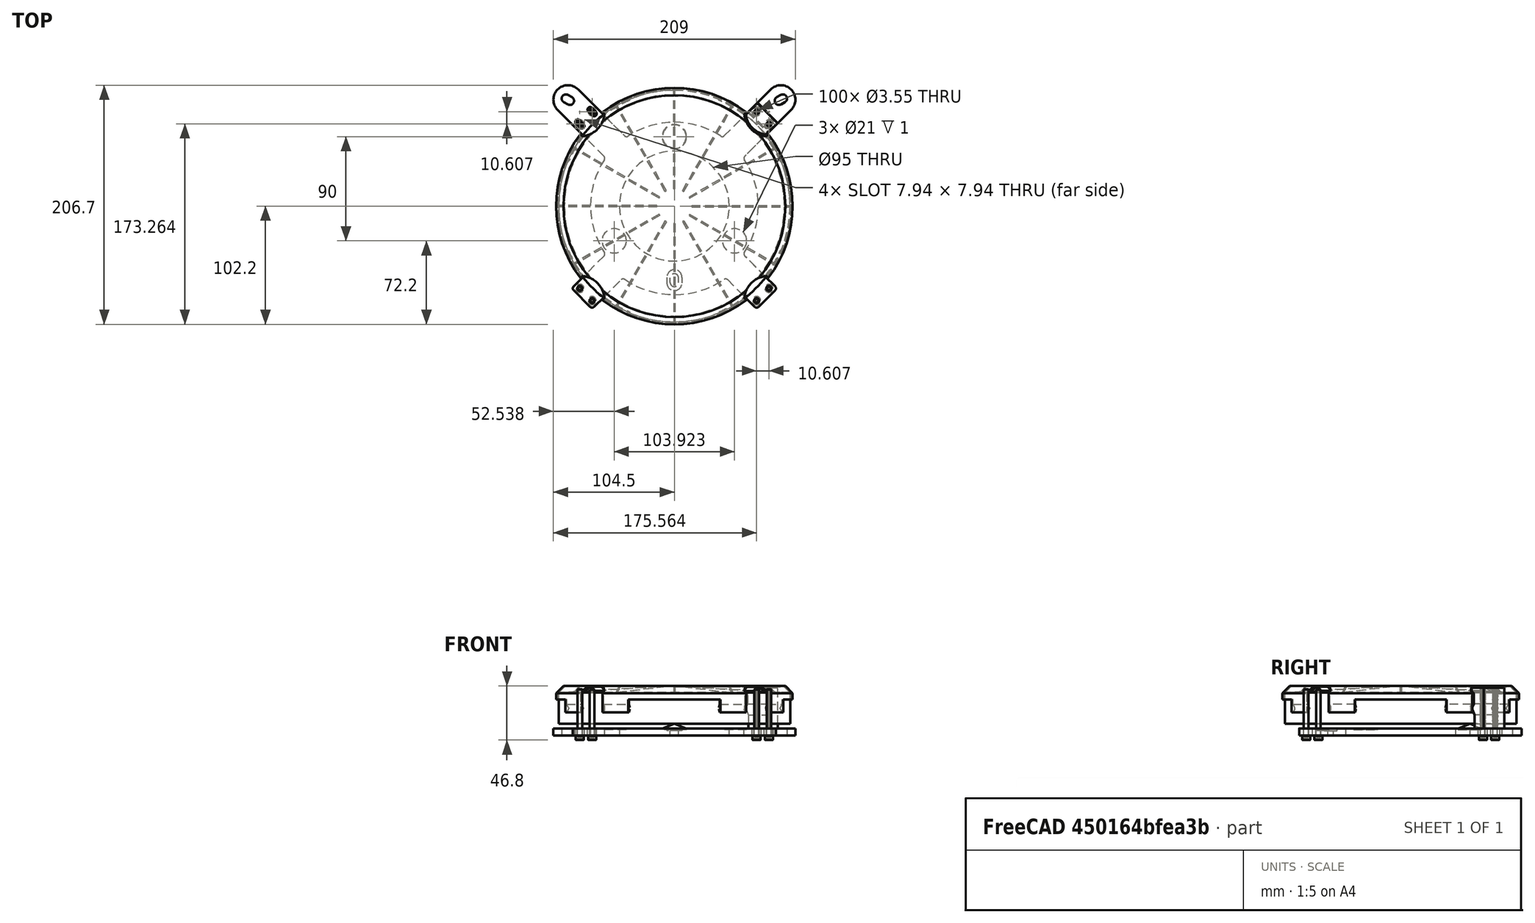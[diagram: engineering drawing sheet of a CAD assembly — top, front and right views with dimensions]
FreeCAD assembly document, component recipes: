
FREECAD ASSEMBLY — COMPONENT RECIPES ("PrimaryMirrorCell")

This assembly document has 5 components, labeled P0..P4 below (a component is one placed body or linked part). 5 of them carry a construction recipe — the FreeCAD feature program that regenerates the part from scratch, quoted from this document or its linked companion documents; the rest are supplied as boundary geometry only. No exploded tour is included for this assembly.
COMPONENT P0 — recipe-attached ("UpperCell", modeled in this document).
Construction recipe (the document's own serialized feature program — sketch geometry with constraints, then the solid features built on it; lengths are millimeters unless a unit is written):

FEATURE [Sketcher::SketchObject] Sketch  label="UpperCell_Base_Sketch"
  FullyConstrained = true
  MapMode = 5
  Support = -> [XY_Plane001]
  expr: Constraints[101] = <<Common>>#<<Parameters>>.collslot
  expr: Constraints[126] = <<Common>>#<<Parameters>>.collbolt * 1.1 + <<Common>>#<<Parameters>>.collextra * 2
  expr: Constraints[31] = <<Common>>#<<Parameters>>.rbracepos + <<Common>>#<<Parameters>>.pri_fwidth / 2
  expr: Constraints[35] = <<Common>>#<<Parameters>>.pri_fwidth
  expr: Constraints[50] = <<Common>>#<<Parameters>>.cpointpos + <<Common>>#<<Parameters>>.pri_fwidth / 2
  expr: Constraints[52] = <<Common>>#<<Parameters>>.pri_mdia / 2 + <<Common>>#<<Parameters>>.pri_mpad_z + <<Common>>#<<Parameters>>.clipwidth
  expr: Constraints[59] = <<Common>>#<<Parameters>>.rbracepos - <<Common>>#<<Parameters>>.pri_fwidth / 2
  expr: Constraints[61] = <<Common>>#<<Parameters>>.rbracepos
  expr: Constraints[76] = -<<Common>>#<<Parameters>>.cpointpos
  expr: Constraints[85] = <<Common>>#<<Parameters>>.collbolt * 1.2
  expr: Constraints[88] = <<Common>>#<<Parameters>>.collpos_y
  sketch-geometry (48):
    g0: LineSegment StartX=-79.9031 StartY=-79.9031 StartZ=0 EndX=92 EndY=92 EndZ=0
    g1: LineSegment StartX=79.9031 StartY=-79.9031 StartZ=0 EndX=-92 EndY=92 EndZ=0
    g2: LineSegment StartX=-59.3364 StartY=-41.6587 StartZ=0 EndX=-88.7419 EndY=-71.0642 EndZ=0
    g3: LineSegment StartX=-88.7419 StartY=-71.0642 StartZ=0 EndX=-71.0642 EndY=-88.7419 EndZ=0
    g4: LineSegment StartX=-71.0642 StartY=-88.7419 StartZ=0 EndX=-44.5278 EndY=-62.2055 EndZ=0
    g5: LineSegment StartX=44.5278 StartY=-62.2055 StartZ=0 EndX=71.0642 EndY=-88.7419 EndZ=0
    g6: LineSegment StartX=71.0642 StartY=-88.7419 StartZ=0 EndX=88.7419 EndY=-71.0642 EndZ=0
    g7: LineSegment StartX=88.7419 StartY=-71.0642 StartZ=0 EndX=59.3364 EndY=-41.6587 EndZ=0
    g8: LineSegment StartX=-59.3364 StartY=41.6587 StartZ=0 EndX=-100.839 EndY=83.1612 EndZ=0
    g9: LineSegment StartX=-100.839 StartY=83.1612 StartZ=0 EndX=-83.1612 EndY=100.839 EndZ=0
    g10: LineSegment StartX=-83.1612 StartY=100.839 StartZ=0 EndX=-41.6587 EndY=59.3364 EndZ=0
    g11: LineSegment StartX=41.6587 StartY=59.3364 StartZ=0 EndX=83.1612 EndY=100.839 EndZ=0
    g12: LineSegment StartX=83.1612 StartY=100.839 StartZ=0 EndX=100.839 EndY=83.1612 EndZ=0
    g13: LineSegment StartX=100.839 StartY=83.1612 StartZ=0 EndX=59.3364 EndY=41.6587 EndZ=0
    g14: ArcOfCircle CenterX=0 CenterY=0 CenterZ=0 NormalX=0 NormalY=0 NormalZ=1 AngleXU=0 Radius=72.5 StartAngle=2.52947 EndAngle=3.75371
    g15: ArcOfCircle CenterX=0 CenterY=0 CenterZ=0 NormalX=0 NormalY=0 NormalZ=1 AngleXU=0 Radius=72.5 StartAngle=5.67107 EndAngle=6.8953
    g16: ArcOfCircle CenterX=0 CenterY=0 CenterZ=0 NormalX=0 NormalY=0 NormalZ=1 AngleXU=0 Radius=72.5 StartAngle=0.958678 EndAngle=2.18291
    g17: ArcOfCircle CenterX=-92 CenterY=92 CenterZ=0 NormalX=0 NormalY=0 NormalZ=1 AngleXU=0 Radius=12.5 StartAngle=0.785398 EndAngle=3.92699
    g18: ArcOfCircle CenterX=92 CenterY=92 CenterZ=0 NormalX=0 NormalY=0 NormalZ=1 AngleXU=0 Radius=12.5 StartAngle=5.49779 EndAngle=8.63938
    g19: ArcOfCircle CenterX=0 CenterY=0 CenterZ=0 NormalX=0 NormalY=0 NormalZ=1 AngleXU=0 Radius=76.5 StartAngle=4.09113 EndAngle=5.33365
    g20: Circle CenterX=0 CenterY=0 CenterZ=0 NormalX=0 NormalY=0 NormalZ=1 AngleXU=0 Radius=47.5
    g21: Circle CenterX=0 CenterY=0 CenterZ=0 NormalX=0 NormalY=0 NormalZ=1 AngleXU=0 Radius=60
    g22: ArcOfCircle CenterX=-93.7367 CenterY=92.992 CenterZ=0 NormalX=0 NormalY=0 NormalZ=1 AngleXU=0 Radius=3.6 StartAngle=1.05182 EndAngle=4.19341
    g23: ArcOfCircle CenterX=-90.2633 CenterY=91.008 CenterZ=0 NormalX=0 NormalY=0 NormalZ=1 AngleXU=0 Radius=3.6 StartAngle=4.19341 EndAngle=7.33501
    g24: LineSegment StartX=-95.5222 StartY=89.866 StartZ=0 EndX=-92.0489 EndY=87.882 EndZ=0
    g25: LineSegment StartX=-91.9511 StartY=96.118 StartZ=0 EndX=-88.4778 EndY=94.134 EndZ=0
    g26: ArcOfCircle CenterX=93.7367 CenterY=92.992 CenterZ=0 NormalX=0 NormalY=0 NormalZ=1 AngleXU=0 Radius=3.6 StartAngle=5.23137 EndAngle=8.37296
    g27: ArcOfCircle CenterX=90.2633 CenterY=91.008 CenterZ=0 NormalX=0 NormalY=0 NormalZ=1 AngleXU=0 Radius=3.6 StartAngle=2.08977 EndAngle=5.23137
    g28: LineSegment StartX=91.9511 StartY=96.118 StartZ=0 EndX=88.4778 EndY=94.134 EndZ=0
    g29: LineSegment StartX=95.5222 StartY=89.866 StartZ=0 EndX=92.0489 EndY=87.882 EndZ=0
    g30: LineSegment StartX=0 StartY=-64 StartZ=0 EndX=92 EndY=92 EndZ=0
    g31: LineSegment StartX=-92 StartY=92 StartZ=0 EndX=0 EndY=-64 EndZ=0
    g32: GeomPoint X=0 Y=60 Z=0
    g33: LineSegment StartX=-95.5222 StartY=89.866 StartZ=0 EndX=-88.4778 EndY=94.134 EndZ=0
    g34: LineSegment StartX=95.5222 StartY=89.866 StartZ=0 EndX=88.4778 EndY=94.134 EndZ=0
    g35: ArcOfCircle CenterX=0 CenterY=-66 CenterZ=0 NormalX=0 NormalY=0 NormalZ=1 AngleXU=0 Radius=3.6 StartAngle=3.14159 EndAngle=6.28319
    g36: ArcOfCircle CenterX=0 CenterY=-62 CenterZ=0 NormalX=0 NormalY=0 NormalZ=1 AngleXU=0 Radius=3.6 StartAngle=8e-16 EndAngle=3.14159
    g37: LineSegment StartX=3.6 StartY=-66 StartZ=0 EndX=3.6 EndY=-62 EndZ=0
    g38: LineSegment StartX=-3.6 StartY=-66 StartZ=0 EndX=-3.6 EndY=-62 EndZ=0
    g39: LineSegment StartX=-3.6 StartY=-62 StartZ=0 EndX=3.6 EndY=-66 EndZ=0
    g40: LineSegment StartX=-92 StartY=92 StartZ=0 EndX=92 EndY=92 EndZ=0
    g41: ArcOfCircle CenterX=92 CenterY=92 CenterZ=0 NormalX=0 NormalY=0 NormalZ=1 AngleXU=0 Radius=12.5 StartAngle=3.14159 EndAngle=4.17955
    g42: LineSegment StartX=79.5 StartY=92 StartZ=0 EndX=81.1459 EndY=85.8001 EndZ=0
    g43: LineSegment StartX=85.6502 StartY=81.2329 StartZ=0 EndX=81.1459 EndY=85.8001 EndZ=0
    g44: LineSegment StartX=92 StartY=92 StartZ=0 EndX=0 EndY=39.4493 EndZ=0
    g45: LineSegment StartX=0 StartY=39.4493 StartZ=0 EndX=-92 EndY=92 EndZ=0
    g46: Circle CenterX=-92 CenterY=92 CenterZ=0 NormalX=0 NormalY=0 NormalZ=1 AngleXU=0 Radius=4.35796
    g47: Circle CenterX=92 CenterY=92 CenterZ=0 NormalX=0 NormalY=0 NormalZ=1 AngleXU=0 Radius=4.35796
  constraints (128):
    c: Perpendicular(g0,g1)
    c: Symmetric(g0,g1,g-2)
    c: Symmetric(g0,g1,g-2)
    c: Coincident(g3,g2)
    c: Coincident(g4,g3)
    c: Coincident(g6,g5)
    c: Coincident(g7,g6)
    c: Coincident(g9,g8)
    c: Coincident(g10,g9)
    c: Coincident(g12,g11)
    c: Coincident(g13,g12)
    c: Parallel(g4,g2)
    c: Parallel(g2,g0)
    c: Parallel(g5,g7)
    c: Parallel(g7,g1)
    c: Perpendicular(g0,g3)
    c: Perpendicular(g1,g6)
    c: Parallel(g8,g10)
    c: Parallel(g10,g1)
    c: Parallel(g11,g13)
    c: Parallel(g13,g0)
    c: Perpendicular(g0,g12)
    c: Perpendicular(g1,g9)
    c: Coincident(g14,g2)
    c: Coincident(g14,g8)
    c: Coincident(g15,g7)
    c: Coincident(g15,g13)
    c: Coincident(g16,g10)
    c: Coincident(g16,g11)
    c: Equal(g16,g14)
    c: Equal(g14,g15)
    c: Radius(g16) = 72.5
    c: Equal(g9,g12)
    c: Equal(g12,g6)
    c: Equal(g6,g3)
    c: Distance(g6) = 25
    c: PointOnObject(g0,g12)
    c: PointOnObject(g1,g9)
    c: Coincident(g17,g1)
    c: Coincident(g17,g9)
    c: Coincident(g17,g8)
    c: Coincident(g18,g0)
    c: Coincident(g18,g11)
    c: Coincident(g18,g12)
    c: PointOnObject(g2,g11)
    c: PointOnObject(g7,g10)
    c: PointOnObject(g0,g3)
    c: PointOnObject(g1,g6)
    c: Coincident(g19,g4)
    c: Coincident(g19,g5)
    c: Radius(g19) = 76.5
    c: PointOnObject(g-1,g0)
    c: Distance(g-1,g0) = 113
    c: Distance(g-1,g18) = 130.108
    c: Coincident(g19,g16)
    c: Coincident(g19,g14)
    c: Coincident(g19,g15)
    c: Coincident(g19,g-1)
    c: Coincident(g20,g14)
    c: Radius(g20) = 47.5
    c: Coincident(g21,g14)
    c: Radius(g21) = 60
    c: Tangent(g22,g25) = 1.5708
    c: Tangent(g22,g24) = -1.5708
    c: Tangent(g24,g23) = -1.5708
    c: Tangent(g25,g23) = 1.5708
    c: Equal(g22,g23)
    c: Tangent(g26,g29) = 1.5708
    c: Tangent(g26,g28) = -1.5708
    c: Tangent(g28,g27) = -1.5708
    c: Tangent(g29,g27) = 1.5708
    c: Equal(g26,g27)
    c: PointOnObject(g30,g-2)
    c: Coincident(g30,g18)
    c: Coincident(g31,g17)
    c: Coincident(g31,g30)
    c: DistanceY(g30) = -64
    c: PointOnObject(g32,g21)
    c: PointOnObject(g32,g-2)
    c: Coincident(g33,g22)
    c: Coincident(g33,g23)
    c: Coincident(g34,g26)
    c: Coincident(g34,g27)
    c: Equal(g28,g25)
    c: Equal(g22,g26)
    c: Diameter(g22) = 7.2
    c: PointOnObject(g18,g34)
    c: PointOnObject(g17,g33)
    c: DistanceY(g17) = 92
    c: Tangent(g35,g38) = 1.5708
    c: Tangent(g35,g37) = -1.5708
    c: Tangent(g37,g36) = -1.5708
    c: Tangent(g38,g36) = 1.5708
    c: Vertical(g37)
    c: Equal(g35,g36)
    c: PointOnObject(g35,g-2)
    c: Equal(g37,g29)
    c: Equal(g36,g27)
    c: Coincident(g39,g36)
    c: Coincident(g39,g35)
    c: PointOnObject(g30,g39)
    c: DistanceY(g38,g38) = 4
    c: Coincident(g40,g17)
    c: Coincident(g40,g18)
    c: Coincident(g41,g18)
    c: PointOnObject(g41,g40)
    c: PointOnObject(g41,g30)
    c: PointOnObject(g41,g18)
    c: Coincident(g42,g41)
    c: PointOnObject(g42,g41)
    c: Coincident(g43,g41)
    c: Coincident(g43,g42)
    c: Coincident(g44,g18)
    c: PointOnObject(g44,g-2)
    c: Coincident(g45,g44)
    c: Coincident(g45,g17)
    c: Equal(g42,g43)
    c: PointOnObject(g42,g44)
    c: PointOnObject(g27,g44)
    c: PointOnObject(g26,g44)
    c: PointOnObject(g23,g45)
    c: PointOnObject(g22,g45)
    c: Angle(g45,g40) = 0.518976
    c: Angle(g40,g30) = 1.03795
    c: Coincident(g46,g1)
    c: Coincident(g47,g0)
    c: Diameter(g47) = 8.71592
    c: Equal(g47,g46)
FEATURE [Sketcher::SketchObject] Sketch011  label="UpperCell_Sketch_cp"
  FullyConstrained = true
  MapMode = 5
  Support = -> [XY_Plane001]
  expr: Constraints[1] = <<Common>>#<<Parameters>>.pri_fwidth
  expr: Constraints[34] = <<Common>>#<<Parameters>>.pri_mdia / 2 + <<Common>>#<<Parameters>>.pri_mpad_z + <<Common>>#<<Parameters>>.clipbolt * 2
  expr: Constraints[3] = <<Common>>#<<Parameters>>.collbolt
  sketch-geometry (22):
    g0: LineSegment StartX=-69.65 StartY=87.3277 StartZ=0 EndX=0 EndY=17.6777 EndZ=0
    g1: LineSegment StartX=0 StartY=17.6777 StartZ=0 EndX=69.65 EndY=87.3277 EndZ=0
    g2: LineSegment StartX=87.3277 StartY=69.65 StartZ=0 EndX=17.6777 EndY=0 EndZ=0
    g3: LineSegment StartX=17.6777 StartY=0 StartZ=0 EndX=87.3277 EndY=-69.65 EndZ=0
    g4: LineSegment StartX=69.65 StartY=-87.3277 StartZ=0 EndX=0 EndY=-17.6777 EndZ=0
    g5: LineSegment StartX=0 StartY=-17.6777 StartZ=0 EndX=-69.65 EndY=-87.3277 EndZ=0
    g6: LineSegment StartX=-87.3277 StartY=-69.65 StartZ=0 EndX=-17.6777 EndY=0 EndZ=0
    g7: LineSegment StartX=-17.6777 StartY=0 StartZ=0 EndX=-87.3277 EndY=69.65 EndZ=0
    g8: LineSegment StartX=-17.6777 StartY=0 StartZ=0 EndX=0 EndY=-17.6777 EndZ=0
    g9: Circle CenterX=0 CenterY=0 CenterZ=0 NormalX=0 NormalY=0 NormalZ=1 AngleXU=0 Radius=3
    g10: LineSegment StartX=-69.65 StartY=87.3277 StartZ=0 EndX=-87.3277 EndY=69.65 EndZ=0
    g11: LineSegment StartX=69.65 StartY=87.3277 StartZ=0 EndX=87.3277 EndY=69.65 EndZ=0
    g12: LineSegment StartX=-87.3277 StartY=-69.65 StartZ=0 EndX=-69.65 EndY=-87.3277 EndZ=0
    g13: LineSegment StartX=69.65 StartY=-87.3277 StartZ=0 EndX=87.3277 EndY=-69.65 EndZ=0
    g14: LineSegment StartX=0 StartY=-17.6777 StartZ=0 EndX=17.6777 EndY=0 EndZ=0
    g15: Circle CenterX=0 CenterY=0 CenterZ=0 NormalX=0 NormalY=0 NormalZ=1 AngleXU=0 Radius=111
    g16: ArcOfCircle CenterX=-78.4889 CenterY=-78.4889 CenterZ=0 NormalX=0 NormalY=0 NormalZ=1 AngleXU=0 Radius=12.5 StartAngle=2.35619 EndAngle=5.49779
    g17: ArcOfCircle CenterX=78.4889 CenterY=-78.4889 CenterZ=0 NormalX=0 NormalY=0 NormalZ=1 AngleXU=0 Radius=12.5 StartAngle=3.92699 EndAngle=7.06858
    g18: ArcOfCircle CenterX=-78.4889 CenterY=78.4889 CenterZ=0 NormalX=0 NormalY=0 NormalZ=1 AngleXU=0 Radius=12.5 StartAngle=0.785398 EndAngle=3.92699
    g19: ArcOfCircle CenterX=78.4889 CenterY=78.4889 CenterZ=0 NormalX=0 NormalY=0 NormalZ=1 AngleXU=0 Radius=12.5 StartAngle=5.49779 EndAngle=8.63938
    g20: LineSegment StartX=78.4889 StartY=78.4889 StartZ=0 EndX=-78.4889 EndY=-78.4889 EndZ=0
    g21: LineSegment StartX=-78.4889 StartY=78.4889 StartZ=0 EndX=78.4889 EndY=-78.4889 EndZ=0
  constraints (58):
    c: Coincident(g1,g0)
    c: Distance(g2,g4) = 25
    c: Coincident(g9,g-1)
    c: Diameter(g9) = 6
    c: Coincident(g10,g0)
    c: Coincident(g10,g7)
    c: Coincident(g13,g4)
    c: Coincident(g13,g3)
    c: Coincident(g11,g2)
    c: Coincident(g1,g11)
    c: Coincident(g6,g12)
    c: Coincident(g12,g5)
    c: Parallel(g5,g13)
    c: Parallel(g13,g10)
    c: Parallel(g10,g1)
    c: Parallel(g1,g2)
    c: Coincident(g6,g7)
    c: PointOnObject(g6,g-1)
    c: PointOnObject(g0,g-2)
    c: Coincident(g4,g5)
    c: Coincident(g4,g8)
    c: PointOnObject(g4,g-2)
    c: Coincident(g2,g3)
    c: PointOnObject(g2,g-1)
    c: Coincident(g8,g6)
    c: Parallel(g11,g0)
    c: Parallel(g0,g7)
    c: Parallel(g8,g12)
    c: Equal(g6,g1)
    c: Equal(g3,g0)
    c: Symmetric(g16,g17,g-2)
    c: Coincident(g14,g4)
    c: Coincident(g14,g2)
    c: Symmetric(g7,g6,g-1)
    c: Radius(g15) = 111
    c: PointOnObject(g16,g15)
    c: Coincident(g15,g9)
    c: Coincident(g16,g6)
    c: Coincident(g16,g5)
    c: Coincident(g17,g4)
    c: Coincident(g17,g3)
    c: PointOnObject(g18,g10)
    c: Coincident(g18,g7)
    c: Coincident(g18,g0)
    c: PointOnObject(g19,g11)
    c: Coincident(g19,g1)
    c: Coincident(g19,g2)
    c: Coincident(g20,g19)
    c: Coincident(g20,g16)
    c: Coincident(g21,g18)
    c: Coincident(g21,g17)
    c: PointOnObject(g9,g20)
    c: PointOnObject(g9,g21)
    c: Perpendicular(g21,g20)
    c: Parallel(g8,g21)
    c: Parallel(g21,g7)
    c: Parallel(g7,g4)
    c: PointOnObject(g16,g12)
FEATURE [PartDesign::Plane] DatumPlane004  label="UpperCell_DatumPlane_Top"
  AttachmentOffset = pos=(0,0,6) rot=(0,0,1;0rad)
  Length = 249.031
  MapMode = 5
  Placement = pos=(0,0,6) rot=(0,0,1;0rad)
  ResizeMode = 0
  Support = -> [XY_Plane001]
  Width = 232.245
  expr: .AttachmentOffset.Base.z = <<Common>>#<<Parameters>>.pri_uthick
FEATURE [Sketcher::SketchObject] Sketch012  label="UpperCell_CollHoles_Sketch"
  FullyConstrained = true
  MapMode = 5
  Placement = pos=(0,0,6) rot=(0,0,1;0rad)
  Support = -> [DatumPlane004]
  expr: Constraints[10] = <<Common>>#<<Parameters>>.collslot + 1
  expr: Constraints[1] = <<Common>>#<<Parameters>>.rbracepos + <<Common>>#<<Parameters>>.collslot
  expr: Constraints[9] = <<Common>>#<<Parameters>>.collbolt * 2 + 1
  sketch-geometry (6):
    g0: GeomPoint X=0 Y=-64 Z=0
    g1: ArcOfCircle CenterX=0 CenterY=-61.5 CenterZ=0 NormalX=0 NormalY=0 NormalZ=1 AngleXU=0 Radius=6.5 StartAngle=2e-16 EndAngle=3.14159
    g2: ArcOfCircle CenterX=0 CenterY=-66.5 CenterZ=0 NormalX=0 NormalY=0 NormalZ=1 AngleXU=0 Radius=6.5 StartAngle=3.14159 EndAngle=6.28319
    g3: LineSegment StartX=-6.5 StartY=-61.5 StartZ=0 EndX=-6.5 EndY=-66.5 EndZ=0
    g4: LineSegment StartX=6.5 StartY=-61.5 StartZ=0 EndX=6.5 EndY=-66.5 EndZ=0
    g5: LineSegment StartX=-6.5 StartY=-61.5 StartZ=0 EndX=6.5 EndY=-66.5 EndZ=0
  constraints (14):
    c: PointOnObject(g0,g-2)
    c: DistanceY(g0,g-1) = 64
    c: Tangent(g1,g4) = 1.5708
    c: Tangent(g1,g3) = -1.5708
    c: Tangent(g3,g2) = -1.5708
    c: Tangent(g4,g2) = 1.5708
    c: Vertical(g3)
    c: Equal(g1,g2)
    c: PointOnObject(g1,g-2)
    c: Diameter(g1) = 13
    c: DistanceY(g4,g4) = 5
    c: Coincident(g5,g1)
    c: Coincident(g5,g2)
    c: PointOnObject(g0,g5)
FEATURE [Sketcher::SketchObject] Sketch017  label="UpperCell_ClipHoles_Sketch"
  FullyConstrained = true
  MapMode = 5
  Placement = pos=(0,0,6) rot=(0,0,1;0rad)
  Support = -> [DatumPlane004]
  expr: Constraints[1] = <<Common>>#<<Parameters>>.pri_mdia / 2 + <<Common>>#<<Parameters>>.pri_mpad_z + <<Common>>#<<Parameters>>.clipwidth / 2 - <<Common>>#<<Parameters>>.clipslot / 2
  expr: Constraints[28] = <<Common>>#<<Parameters>>.clipbolt * 1.1
  expr: Constraints[47] = <<Common>>#<<Parameters>>.clipslot
  expr: Constraints[58] = <<Common>>#<<Parameters>>.clipslot / 2
  expr: Constraints[9] = <<Common>>#<<Parameters>>.pri_fwidth - <<Common>>#<<Parameters>>.clipbolt * 2.5
  sketch-geometry (28):
    g0: Circle CenterX=0 CenterY=0 CenterZ=0 NormalX=0 NormalY=0 NormalZ=1 AngleXU=0 Radius=105.5
    g1: LineSegment StartX=-76.3675 StartY=-76.3675 StartZ=0 EndX=74.5998 EndY=74.5998 EndZ=0
    g2: LineSegment StartX=-74.5998 StartY=74.5998 StartZ=0 EndX=76.3675 EndY=-76.3675 EndZ=0
    g3: LineSegment StartX=-81.6708 StartY=-71.0642 StartZ=0 EndX=-71.0642 EndY=-81.6708 EndZ=0
    g4: LineSegment StartX=71.0642 StartY=-81.6708 StartZ=0 EndX=81.6708 EndY=-71.0642 EndZ=0
    g5: LineSegment StartX=69.2965 StartY=79.9031 StartZ=0 EndX=79.9031 EndY=69.2965 EndZ=0
    g6: LineSegment StartX=-69.2965 StartY=79.9031 StartZ=0 EndX=-79.9031 EndY=69.2965 EndZ=0
    g7: ArcOfCircle CenterX=72.832 CenterY=83.4386 CenterZ=0 NormalX=0 NormalY=0 NormalZ=1 AngleXU=0 Radius=2.2 StartAngle=5.49779 EndAngle=8.63938
    g8: ArcOfCircle CenterX=69.2965 CenterY=79.9031 CenterZ=0 NormalX=0 NormalY=0 NormalZ=1 AngleXU=0 Radius=2.2 StartAngle=2.35619 EndAngle=5.49779
    g9: LineSegment StartX=71.2764 StartY=84.9942 StartZ=0 EndX=67.7408 EndY=81.4587 EndZ=0
    g10: LineSegment StartX=74.3876 StartY=81.883 StartZ=0 EndX=70.8521 EndY=78.3474 EndZ=0
    g11: ArcOfCircle CenterX=83.4386 CenterY=72.832 CenterZ=0 NormalX=0 NormalY=0 NormalZ=1 AngleXU=0 Radius=2.2 StartAngle=5.49779 EndAngle=8.63938
    g12: ArcOfCircle CenterX=79.9031 CenterY=69.2965 CenterZ=0 NormalX=0 NormalY=0 NormalZ=1 AngleXU=0 Radius=2.2 StartAngle=2.35619 EndAngle=5.49779
    g13: LineSegment StartX=81.883 StartY=74.3876 StartZ=0 EndX=78.3474 EndY=70.8521 EndZ=0
    g14: LineSegment StartX=84.9942 StartY=71.2764 StartZ=0 EndX=81.4587 EndY=67.7408 EndZ=0
    g15: ArcOfCircle CenterX=-72.832 CenterY=83.4386 CenterZ=0 NormalX=0 NormalY=0 NormalZ=1 AngleXU=0 Radius=2.2 StartAngle=0.785398 EndAngle=3.92699
    g16: ArcOfCircle CenterX=-69.2965 CenterY=79.9031 CenterZ=0 NormalX=0 NormalY=0 NormalZ=1 AngleXU=0 Radius=2.2 StartAngle=3.92699 EndAngle=7.06858
    g17: LineSegment StartX=-74.3876 StartY=81.883 StartZ=0 EndX=-70.8521 EndY=78.3474 EndZ=0
    g18: LineSegment StartX=-71.2764 StartY=84.9942 StartZ=0 EndX=-67.7408 EndY=81.4587 EndZ=0
    g19: ArcOfCircle CenterX=-83.4386 CenterY=72.832 CenterZ=0 NormalX=0 NormalY=0 NormalZ=1 AngleXU=0 Radius=2.2 StartAngle=0.785398 EndAngle=3.92699
    g20: ArcOfCircle CenterX=-79.9031 CenterY=69.2965 CenterZ=0 NormalX=0 NormalY=0 NormalZ=1 AngleXU=0 Radius=2.2 StartAngle=3.92699 EndAngle=7.06858
    g21: LineSegment StartX=-84.9942 StartY=71.2764 StartZ=0 EndX=-81.4587 EndY=67.7408 EndZ=0
    g22: LineSegment StartX=-81.883 StartY=74.3876 StartZ=0 EndX=-78.3474 EndY=70.8521 EndZ=0
    g23: GeomPoint X=-74.5998 Y=-74.5998 Z=0
    g24: Circle CenterX=81.6708 CenterY=-71.0642 CenterZ=0 NormalX=0 NormalY=0 NormalZ=1 AngleXU=0 Radius=2.2
    g25: Circle CenterX=71.0642 CenterY=-81.6708 CenterZ=0 NormalX=0 NormalY=0 NormalZ=1 AngleXU=0 Radius=2.2
    g26: Circle CenterX=-71.0642 CenterY=-81.6708 CenterZ=0 NormalX=0 NormalY=0 NormalZ=1 AngleXU=0 Radius=2.2
    g27: Circle CenterX=-81.6708 CenterY=-71.0642 CenterZ=0 NormalX=0 NormalY=0 NormalZ=1 AngleXU=0 Radius=2.2
  constraints (67):
    c: Coincident(g0,g-1)
    c: Radius(g0) = 105.5
    c: PointOnObject(g1,g0)
    c: PointOnObject(g2,g0)
    c: PointOnObject(g-1,g1)
    c: PointOnObject(g-1,g2)
    c: Perpendicular(g2,g1)
    c: Symmetric(g1,g2,g-2)
    c: Symmetric(g3,g3,g1)
    c: Distance(g3) = 15
    c: Symmetric(g4,g4,g2)
    c: Symmetric(g6,g6,g2)
    c: Symmetric(g5,g5,g1)
    c: PointOnObject(g1,g5)
    c: PointOnObject(g2,g6)
    c: Equal(g6,g5)
    c: Equal(g5,g4)
    c: Equal(g4,g3)
    c: Tangent(g7,g10) = 1.5708
    c: Tangent(g7,g9) = -1.5708
    c: Tangent(g9,g8) = -1.5708
    c: Tangent(g10,g8) = 1.5708
    c: Equal(g7,g8)
    c: Tangent(g11,g14) = 1.5708
    c: Tangent(g11,g13) = -1.5708
    c: Tangent(g13,g12) = -1.5708
    c: Tangent(g14,g12) = 1.5708
    c: Equal(g11,g12)
    c: Diameter(g7) = 4.4
    c: Equal(g11,g7)
    c: Equal(g14,g10)
    c: Tangent(g15,g18) = 1.5708
    c: Tangent(g15,g17) = -1.5708
    c: Tangent(g17,g16) = -1.5708
    c: Tangent(g18,g16) = 1.5708
    c: Equal(g15,g16)
    c: Tangent(g19,g22) = 1.5708
    c: Tangent(g19,g21) = -1.5708
    c: Tangent(g21,g20) = -1.5708
    c: Tangent(g22,g20) = 1.5708
    c: Equal(g19,g20)
    c: Equal(g7,g15)
    c: Equal(g15,g19)
    c: Equal(g10,g17)
    c: Equal(g21,g17)
    c: Parallel(g9,g13)
    c: Parallel(g13,g1)
    c: Distance(g10) = 5
    c: Coincident(g8,g5)
    c: Coincident(g12,g5)
    c: Parallel(g17,g21)
    c: Parallel(g21,g2)
    c: Coincident(g16,g6)
    c: Coincident(g20,g6)
    c: PointOnObject(g23,g0)
    c: PointOnObject(g2,g4)
    c: PointOnObject(g1,g3)
    c: PointOnObject(g23,g1)
    c: Distance(g1,g23) = 2.5
    c: Coincident(g24,g4)
    c: Coincident(g25,g4)
    c: Coincident(g26,g3)
    c: Coincident(g27,g3)
    c: Equal(g27,g26)
    c: Equal(g26,g25)
    c: Equal(g25,g24)
    c: Equal(g24,g7)
FEATURE [Sketcher::SketchObject] Sketch024  label="UpperCell_MountHoles_Sketch"
  FullyConstrained = true
  MapMode = 5
  Placement = pos=(0,0,6) rot=(0,0,1;0rad)
  Support = -> [DatumPlane004]
  expr: Constraints[1] = <<Common>>#<<Parameters>>.rbracepos
  expr: Constraints[8] = <<Common>>#<<Parameters>>.pri_fwidth - 4
  sketch-geometry (6):
    g0: Circle CenterX=0 CenterY=0 CenterZ=0 NormalX=0 NormalY=0 NormalZ=1 AngleXU=0 Radius=60
    g1: LineSegment StartX=-51.9615 StartY=-30 StartZ=0 EndX=0 EndY=0 EndZ=0
    g2: LineSegment StartX=0 StartY=0 StartZ=0 EndX=51.9615 EndY=-30 EndZ=0
    g3: Circle CenterX=0 CenterY=60 CenterZ=0 NormalX=0 NormalY=0 NormalZ=1 AngleXU=0 Radius=10.5
    g4: Circle CenterX=-51.9615 CenterY=-30 CenterZ=0 NormalX=0 NormalY=0 NormalZ=1 AngleXU=0 Radius=10.5
    g5: Circle CenterX=51.9615 CenterY=-30 CenterZ=0 NormalX=0 NormalY=0 NormalZ=1 AngleXU=0 Radius=10.5
  constraints (14):
    c: Coincident(g0,g-1)
    c: Radius(g0) = 60
    c: Coincident(g1,g-1)
    c: Coincident(g2,g-1)
    c: Angle(g1,g2) = 2.0944
    c: PointOnObject(g2,g0)
    c: Symmetric(g1,g2,g-2)
    c: PointOnObject(g3,g-2)
    c: Diameter(g3) = 21
    c: PointOnObject(g3,g0)
    c: Coincident(g4,g1)
    c: Coincident(g5,g2)
    c: Equal(g5,g4)
    c: Equal(g4,g3)
FEATURE [PartDesign::CoordinateSystem] Local_CS006  label="LCS_UpperCell_Pad_A"
  AttacherType = Attacher::AttachEngine3D
  AttachmentOffset = pos=(0,60,-1) rot=(0,0,1;0rad)
  MapMode = 5
  Placement = pos=(0,60,5) rot=(0,0,1;0rad)
  Support = -> [DatumPlane004]
  expr: .AttachmentOffset.Base.y = <<Common>>#<<Parameters>>.rbracepos
FEATURE [PartDesign::CoordinateSystem] Local_CS007  label="LCS_UpperCell_Pad_FP"
  AttacherType = Attacher::AttachEngine3D
  AttachmentOffset = pos=(51.9615,-30,-1) rot=(0,0,-1;2.0944rad)
  MapMode = 5
  Placement = pos=(51.9615,-30,5) rot=(0,0,-1;2.0944rad)
  Support = -> [DatumPlane004]
  expr: .AttachmentOffset.Base.x = <<Common>>#<<Parameters>>.rbracepos * sin(120 deg)
  expr: .AttachmentOffset.Base.y = <<Common>>#<<Parameters>>.rbracepos * cos(120 deg)
FEATURE [PartDesign::CoordinateSystem] Local_CS008  label="LCS_UpperCell_Pad_FS"
  AttacherType = Attacher::AttachEngine3D
  AttachmentOffset = pos=(-51.9615,-30,-1) rot=(0,0,1;2.0944rad)
  MapMode = 5
  Placement = pos=(-51.9615,-30,5) rot=(0,0,1;2.0944rad)
  Support = -> [DatumPlane004]
  expr: .AttachmentOffset.Base.x = <<Common>>#<<Parameters>>.rbracepos * sin(-120 deg)
  expr: .AttachmentOffset.Base.y = <<Common>>#<<Parameters>>.rbracepos * cos(-120 deg)
FEATURE [PartDesign::CoordinateSystem] Local_CS009  label="LCS_UpperCell_CollBoltF"
  AttacherType = Attacher::AttachEngine3D
  AttachmentOffset = pos=(0,-64,-2) rot=(0,0,1;0rad)
  MapMode = 5
  Placement = pos=(0,-64,4) rot=(0,0,1;0rad)
  Support = -> [DatumPlane004]
  expr: .AttachmentOffset.Base.y = -<<Common>>#<<Parameters>>.cpointpos
FEATURE [PartDesign::CoordinateSystem] Local_CS010  label="LCS_UpperCell_CollBolt_AS"
  AttacherType = Attacher::AttachEngine3D
  AttachmentOffset = pos=(-92,92,0) rot=(0,0,1;0rad)
  MapMode = 5
  Placement = pos=(-92,92,6) rot=(0,0,1;0rad)
  Support = -> [DatumPlane004]
  expr: .AttachmentOffset.Base.x = -<<Common>>#<<Parameters>>.collpos_y
  expr: .AttachmentOffset.Base.y = <<Common>>#<<Parameters>>.collpos_y
FEATURE [PartDesign::CoordinateSystem] Local_CS011  label="LCS_UpperCell_CollBolt_AP"
  AttacherType = Attacher::AttachEngine3D
  AttachmentOffset = pos=(92,92,0) rot=(0,0,1;0rad)
  MapMode = 5
  Placement = pos=(92,92,6) rot=(0,0,1;0rad)
  Support = -> [DatumPlane004]
  expr: .AttachmentOffset.Base.x = <<Common>>#<<Parameters>>.collpos_y
  expr: .AttachmentOffset.Base.y = <<Common>>#<<Parameters>>.collpos_y
FEATURE [PartDesign::Pad] Pad021  label="UpperCell_pad"
  Direction = (0,0,1)
  Length = 6
  Length2 = 100
  Profile = -> Sketch
  Type = 0
  expr: Length = <<Common>>#<<Parameters>>.pri_uthick
FEATURE [PartDesign::CoordinateSystem] Local_CS005  label="LCS_UpperCell_Mirror"
  AttacherType = Attacher::AttachEngine3D
  AttachmentOffset = pos=(0,0,4) rot=(0,0,1;0rad)
  MapMode = 11
  Placement = pos=(0,0,10) rot=(0,0,1;1.5708rad)
  Support = -> [Pad021]
  expr: .AttachmentOffset.Base.z = <<Common>>#<<Parameters>>.pri_mpad_r
FEATURE [PartDesign::CoordinateSystem] Local_CS012  label="LCS_UpperCell_Base"
  AttacherType = Attacher::AttachEngine3D
  AttachmentOffset = pos=(0,0,0) rot=(0,0,-1;1.5708rad)
  MapMode = 11
  Support = -> [Pad021]
FEATURE [PartDesign::CoordinateSystem] Local_CS080  label="LCS_UpperCell_Clip_AS"
  AttacherType = Attacher::AttachEngine3D
  AttachmentOffset = pos=(-76.3675,76.3675,0) rot=(0,0,-1;2.35619rad)
  MapMode = 5
  Placement = pos=(-76.3675,76.3675,6) rot=(0,0,-1;2.35619rad)
  Support = -> [DatumPlane004]
  expr: .AttachmentOffset.Base.x = -(<<Common>>#<<Parameters>>.pri_mdia / 2 + <<Common>>#<<Parameters>>.pri_mpad_z + <<Common>>#<<Parameters>>.clipwidth / 2) / sqrt(2)
  expr: .AttachmentOffset.Base.y = (<<Common>>#<<Parameters>>.pri_mdia / 2 + <<Common>>#<<Parameters>>.pri_mpad_z + <<Common>>#<<Parameters>>.clipwidth / 2) / sqrt(2)
FEATURE [PartDesign::CoordinateSystem] Local_CS081  label="LCS_UpperCell_Clip_AP"
  AttacherType = Attacher::AttachEngine3D
  AttachmentOffset = pos=(76.3675,76.3675,0) rot=(0,0,1;2.35619rad)
  MapMode = 5
  Placement = pos=(76.3675,76.3675,6) rot=(0,0,1;2.35619rad)
  Support = -> [DatumPlane004]
  expr: .AttachmentOffset.Base.x = (<<Common>>#<<Parameters>>.pri_mdia / 2 + <<Common>>#<<Parameters>>.pri_mpad_z + <<Common>>#<<Parameters>>.clipwidth / 2) / sqrt(2)
  expr: .AttachmentOffset.Base.y = (<<Common>>#<<Parameters>>.pri_mdia / 2 + <<Common>>#<<Parameters>>.pri_mpad_z + <<Common>>#<<Parameters>>.clipwidth / 2) / sqrt(2)
FEATURE [PartDesign::CoordinateSystem] Local_CS082  label="LCS_UpperCell_Clip_FP"
  AttacherType = Attacher::AttachEngine3D
  AttachmentOffset = pos=(76.3675,-76.3675,0) rot=(0,0,1;0.785398rad)
  MapMode = 5
  Placement = pos=(76.3675,-76.3675,6) rot=(0,0,1;0.785398rad)
  Support = -> [DatumPlane004]
  expr: .AttachmentOffset.Base.x = (<<Common>>#<<Parameters>>.pri_mdia / 2 + <<Common>>#<<Parameters>>.pri_mpad_z + <<Common>>#<<Parameters>>.clipwidth / 2) / sqrt(2)
  expr: .AttachmentOffset.Base.y = -(<<Common>>#<<Parameters>>.pri_mdia / 2 + <<Common>>#<<Parameters>>.pri_mpad_z + <<Common>>#<<Parameters>>.clipwidth / 2) / sqrt(2)
FEATURE [PartDesign::CoordinateSystem] Local_CS083  label="LCS_UpperCell_Clip_FS"
  AttacherType = Attacher::AttachEngine3D
  AttachmentOffset = pos=(-76.3675,-76.3675,0) rot=(0,0,-1;0.785398rad)
  MapMode = 5
  Placement = pos=(-76.3675,-76.3675,6) rot=(0,0,-1;0.785398rad)
  Support = -> [DatumPlane004]
  expr: .AttachmentOffset.Base.x = -(<<Common>>#<<Parameters>>.pri_mdia / 2 + <<Common>>#<<Parameters>>.pri_mpad_z + <<Common>>#<<Parameters>>.clipwidth / 2) / sqrt(2)
  expr: .AttachmentOffset.Base.y = -(<<Common>>#<<Parameters>>.pri_mdia / 2 + <<Common>>#<<Parameters>>.pri_mpad_z + <<Common>>#<<Parameters>>.clipwidth / 2) / sqrt(2)
FEATURE [PartDesign::Pocket] Pocket013  label="UpperCell_ClipHoles_Cut"
  BaseFeature = -> Pad021
  Direction = (0,0,-1)
  Length = 5
  Length2 = 100
  Profile = -> Sketch017
  Type = 1
FEATURE [PartDesign::Pocket] Pocket014  label="UpperCell_CollHoles_Cut"
  BaseFeature = -> Pocket013
  Direction = (0,0,-1)
  Length = 2
  Length2 = 100
  Profile = -> Sketch012
  Type = 0
FEATURE [PartDesign::CoordinateSystem] Local_CS114  label="LCS_UpperCell_CBolt_FSS"
  AttacherType = Attacher::AttachEngine3D
  AttachmentOffset = pos=(7.5,0,6) rot=(0,0,1;0rad)
  MapMode = 5
  Placement = pos=(-81.6708,-71.0642,0) rot=(0.382683,0.92388,0;3.14159rad)
  Support = -> [Local_CS083]
  expr: .AttachmentOffset.Base.x = (<<Common>>#<<Parameters>>.pri_fwidth - <<Common>>#<<Parameters>>.clipbolt * 2.5) / 2
  expr: .AttachmentOffset.Base.z = <<Common>>#<<Parameters>>.pri_uthick
FEATURE [PartDesign::CoordinateSystem] Local_CS115  label="LCS_UpperCell_CBolt_FSP"
  AttacherType = Attacher::AttachEngine3D
  AttachmentOffset = pos=(-7.5,0,6) rot=(0,0,1;0rad)
  MapMode = 5
  Placement = pos=(-71.0642,-81.6708,0) rot=(0.382683,0.92388,0;3.14159rad)
  Support = -> [Local_CS083]
  expr: .AttachmentOffset.Base.x = -(<<Common>>#<<Parameters>>.pri_fwidth - <<Common>>#<<Parameters>>.clipbolt * 2.5) / 2
  expr: .AttachmentOffset.Base.z = <<Common>>#<<Parameters>>.pri_uthick
FEATURE [PartDesign::CoordinateSystem] Local_CS116  label="LCS_UpperCell_CBolt_FPS"
  AttacherType = Attacher::AttachEngine3D
  AttachmentOffset = pos=(7.5,0,6) rot=(0,0,1;0rad)
  MapMode = 5
  Placement = pos=(71.0642,-81.6708,0) rot=(-0.382683,0.92388,0;3.14159rad)
  Support = -> [Local_CS082]
  expr: .AttachmentOffset.Base.x = (<<Common>>#<<Parameters>>.pri_fwidth - <<Common>>#<<Parameters>>.clipbolt * 2.5) / 2
  expr: .AttachmentOffset.Base.z = <<Common>>#<<Parameters>>.pri_uthick
FEATURE [PartDesign::CoordinateSystem] Local_CS117  label="LCS_UpperCell_CBolt_FPP"
  AttacherType = Attacher::AttachEngine3D
  AttachmentOffset = pos=(-7.5,0,6) rot=(0,0,1;0rad)
  MapMode = 5
  Placement = pos=(81.6708,-71.0642,0) rot=(-0.382683,0.92388,0;3.14159rad)
  Support = -> [Local_CS082]
  expr: .AttachmentOffset.Base.x = -(<<Common>>#<<Parameters>>.pri_fwidth - <<Common>>#<<Parameters>>.clipbolt * 2.5) / 2
  expr: .AttachmentOffset.Base.z = <<Common>>#<<Parameters>>.pri_uthick
FEATURE [PartDesign::CoordinateSystem] Local_CS118  label="LCS_UpperCell_CBolt_ASS"
  AttacherType = Attacher::AttachEngine3D
  AttachmentOffset = pos=(-7.5,0,6) rot=(0,0,1;0rad)
  MapMode = 5
  Placement = pos=(-81.6708,71.0642,0) rot=(0.92388,0.382683,0;3.14159rad)
  Support = -> [Local_CS080]
  expr: .AttachmentOffset.Base.x = -(<<Common>>#<<Parameters>>.pri_fwidth - <<Common>>#<<Parameters>>.clipbolt * 2.5) / 2
  expr: .AttachmentOffset.Base.z = <<Common>>#<<Parameters>>.pri_uthick
FEATURE [PartDesign::CoordinateSystem] Local_CS119  label="LCS_UpperCell_CBolt_ASP"
  AttacherType = Attacher::AttachEngine3D
  AttachmentOffset = pos=(7.5,0,6) rot=(0,0,1;0rad)
  MapMode = 5
  Placement = pos=(-71.0642,81.6708,0) rot=(0.92388,0.382683,0;3.14159rad)
  Support = -> [Local_CS080]
  expr: .AttachmentOffset.Base.x = (<<Common>>#<<Parameters>>.pri_fwidth - <<Common>>#<<Parameters>>.clipbolt * 2.5) / 2
  expr: .AttachmentOffset.Base.z = <<Common>>#<<Parameters>>.pri_uthick
FEATURE [PartDesign::CoordinateSystem] Local_CS120  label="LCS_UpperCell_CBolt_APP"
  AttacherType = Attacher::AttachEngine3D
  AttachmentOffset = pos=(7.5,0,6) rot=(0,0,1;0rad)
  MapMode = 5
  Placement = pos=(81.6708,71.0642,0) rot=(0.92388,-0.382683,0;3.14159rad)
  Support = -> [Local_CS081]
  expr: .AttachmentOffset.Base.x = (<<Common>>#<<Parameters>>.pri_fwidth - <<Common>>#<<Parameters>>.clipbolt * 2.5) / 2
  expr: .AttachmentOffset.Base.z = <<Common>>#<<Parameters>>.pri_uthick
FEATURE [PartDesign::CoordinateSystem] Local_CS121  label="LCS_UpperCell_CBolt_APS"
  AttacherType = Attacher::AttachEngine3D
  AttachmentOffset = pos=(-7.5,0,6) rot=(0,0,1;0rad)
  MapMode = 5
  Placement = pos=(71.0642,81.6708,0) rot=(0.92388,-0.382683,0;3.14159rad)
  Support = -> [Local_CS081]
  expr: .AttachmentOffset.Base.x = -(<<Common>>#<<Parameters>>.pri_fwidth - <<Common>>#<<Parameters>>.clipbolt * 2.5) / 2
  expr: .AttachmentOffset.Base.z = <<Common>>#<<Parameters>>.pri_uthick
FEATURE [PartDesign::Fillet] Fillet  label="UpperCell_Fillet"
  Base = -> Pocket014 [Edge1,Edge2,Edge8,Edge128,Edge136,Edge137,Edge129,Edge106,Edge108,Edge114,Edge113,Edge107,Edge105,Edge104,Edge110,Edge112]
  BaseFeature = -> Pocket014
  Radius = 2.5
  SupportTransform = false
  UseAllEdges = false
  expr: Radius = <<Common>>#<<Parameters>>.pri_fillet
FEATURE [PartDesign::Pocket] Pocket036  label="UpperCell_MountHoles"
  BaseFeature = -> Fillet
  Direction = (0,0,-1)
  Length = 1
  Length2 = 100
  Profile = -> Sketch024
  Type = 0
FEATURE [PartDesign::Body] Body  label="UpperCell"
  Group = -> [Sketch,Sketch011,Sketch012,Sketch017,DatumPlane004,Sketch024,Local_CS005,Local_CS006,Local_CS007,Local_CS008,Local_CS009,Local_CS010,Local_CS011,Local_CS012,Pad021,Local_CS080,Local_CS081,Local_CS082,Local_CS083,Pocket013,Pocket014,Local_CS114,Local_CS115,Local_CS116,Local_CS117,Local_CS118,Local_CS119,Local_CS120,Local_CS121,Fillet,Pocket036]
  Origin = -> Origin001
  Placement = pos=(0,0,-37) rot=(0,0,1;0rad)
  Tip = -> Pocket036
  expr: .Placement.Base.z = <<Common>>#<<Parameters>>.datum_uppercell
COMPONENT P1 — recipe-attached ("LowerPad", modeled in this document).
Construction recipe (the document's own serialized feature program — sketch geometry with constraints, then the solid features built on it; lengths are millimeters unless a unit is written):

FEATURE [Sketcher::SketchObject] Sketch026  label="LowerPad_Profile_Sketch"
  FullyConstrained = true
  MapMode = 5
  Placement = pos=(0,0,0) rot=(1,0,0;1.5708rad)
  Support = -> [XZ_Plane006]
  expr: Constraints[13] = <<Common>>#<<Parameters>>.pri_mpad_r + 1
  expr: Constraints[1] = <<Common>>#<<Parameters>>.pri_fwidth / 2 - 2.25
  sketch-geometry (5):
    g0: LineSegment StartX=1e-16 StartY=4 StartZ=0 EndX=1e-16 EndY=-1 EndZ=0
    g1: LineSegment StartX=1e-16 StartY=-1 StartZ=0 EndX=10.25 EndY=-1 EndZ=0
    g2: LineSegment StartX=10.25 StartY=-1 StartZ=0 EndX=10.25 EndY=0 EndZ=0
    g3: LineSegment StartX=10.25 StartY=0 StartZ=0 EndX=0.751862 EndY=3.8533 EndZ=0
    g4: ArcOfCircle CenterX=0 CenterY=2 CenterZ=0 NormalX=0 NormalY=0 NormalZ=1 AngleXU=0 Radius=2 StartAngle=1.18539 EndAngle=1.5708
  constraints (15):
    c: Vertical(g0)
    c: DistanceX(g1,g1) = 10.25
    c: Coincident(g2,g1)
    c: Vertical(g2)
    c: Coincident(g3,g2)
    c: PointOnObject(g4,g0)
    c: Coincident(g4,g0)
    c: Diameter(g4) = 4
    c: Tangent(g4,g3) = -1.5708
    c: Horizontal(g1)
    c: Coincident(g0,g1)
    c: PointOnObject(g0,g-2)
    c: DistanceY(g2,g2) = 1
    c: DistanceY(g0,g0) = 5
    c: PointOnObject(g2,g-1)
FEATURE [PartDesign::Revolution] Revolution  label="LowerPad_Revolution"
  Angle = 360
  Axis = (0,-2e-16,1)
  Base = (0,0,0)
  Placement = pos=(0,0,0) rot=(1,0,0;1.5708rad)
  Profile = -> Sketch026
  ReferenceAxis = -> Sketch026 [V_Axis]
  Reversed = true
FEATURE [PartDesign::CoordinateSystem] Local_CS002  label="LCS_PadBase"
  AttacherType = Attacher::AttachEngine3D
  MapMode = 11
  Placement = pos=(0,0,-1) rot=(0,0,1;1.5708rad)
  Support = -> [Revolution]
FEATURE [PartDesign::CoordinateSystem] Local_CS004  label="LCS_PadUpper"
  AttacherType = Attacher::AttachEngine3D
  MapMode = 11
  Placement = pos=(0,0,3.8533) rot=(0.707107,-0.707107,0;3.14159rad)
  Support = -> [Revolution]
FEATURE [PartDesign::Body] Body002  label="LowerPad"
  Group = -> [Sketch026,Revolution,Local_CS002,Local_CS004]
  Origin = -> Origin006
  Placement = pos=(0,60,-31) rot=(0,0,1;0rad)
  Tip = -> Revolution
  expr: .Placement.Base.y = <<Common>>#<<Parameters>>.rbracepos
  expr: .Placement.Base.z = <<Common>>#<<Parameters>>.datum_uppercell + <<Common>>#<<Parameters>>.pri_uthick
COMPONENT P2 — recipe-attached ("PrimaryMirror", modeled in this document).
Construction recipe (the document's own serialized feature program — sketch geometry with constraints, then the solid features built on it; lengths are millimeters unless a unit is written):

FEATURE [PartDesign::CoordinateSystem] Local_CS  label="LCS_MirrorFace"
  AttacherType = Attacher::AttachEngine3D
  MapMode = 5
  Support = -> [XY_Plane]
FEATURE [PartDesign::CoordinateSystem] Local_CS001  label="LCS_MirrorBase"
  AttacherType = Attacher::AttachEngine3D
  AttachmentOffset = pos=(0,0,-27) rot=(0,0,1;0rad)
  MapMode = 5
  Placement = pos=(0,0,-27) rot=(0,0,1;0rad)
  Support = -> [XY_Plane]
  expr: .AttachmentOffset.Base.z = -<<Common>>#<<Parameters>>.pri_mthick
FEATURE [PartDesign::CoordinateSystem] Local_CS039  label="LCS_SecondaryMirror"
  AttacherType = Attacher::AttachEngine3D
  AttachmentOffset = pos=(0,0,835) rot=(0,0,1;0rad)
  MapMode = 5
  Placement = pos=(0,0,835) rot=(0,0,1;0rad)
  Support = -> [XY_Plane]
  expr: .AttachmentOffset.Base.z = <<Common>>#<<Parameters>>.mirror_distance
FEATURE [Sketcher::SketchObject] Sketch116  label="PriMirror_Profile"
  FullyConstrained = true
  MapMode = 5
  Placement = pos=(0,0,0) rot=(0.57735,0.57735,0.57735;2.0944rad)
  Support = -> [YZ_Plane]
  expr: Constraints[12] = <<Common>>#<<Parameters>>.pri_mdia / 2
  expr: Constraints[13] = <<Common>>#<<Parameters>>.pri_mthick
  expr: Constraints[14] = <<Common>>#<<Parameters>>.sys_flen
  sketch-geometry (6):
    g0: LineSegment StartX=0 StartY=-27 StartZ=0 EndX=100 EndY=-27 EndZ=0
    g1: LineSegment StartX=100 StartY=-27 StartZ=0 EndX=100 EndY=0 EndZ=0
    g2: LineSegment StartX=1.2212e-12 StartY=-2.5 StartZ=0 EndX=0 EndY=-27 EndZ=0
    g3: ArcOfParabola CenterX=1.2212e-12 CenterY=-2.5 CenterZ=0 NormalX=0 NormalY=0 NormalZ=1 Focal=1000 AngleXU=1.5708 StartAngle=-100 EndAngle=0
    g4: GeomPoint X=1.2212e-12 Y=997.5 Z=0
    g5: LineSegment StartX=1.2212e-12 StartY=-2.5 StartZ=0 EndX=1.2212e-12 EndY=997.5 EndZ=0
  constraints (16):
    c: PointOnObject(g0,g-2)
    c: Horizontal(g0)
    c: Coincident(g1,g0)
    c: PointOnObject(g1,g-1)
    c: Vertical(g1)
    c: PointOnObject(g2,g-2)
    c: Coincident(g2,g0)
    c: InternalAlignment(g4,g3)
    c: InternalAlignment(g5,g3)
    c: PointOnObject(g4,g-2)
    c: Coincident(g3,g1)
    c: Coincident(g2,g3)
    c: DistanceX(g0,g0) = 100
    c: DistanceY(g1,g1) = 27
    c: DistanceY(g5,g5) = 1000
    c: Vertical(g5)
FEATURE [PartDesign::Revolution] Revolution003  label="PrimaryMirror_Revolution"
  Angle = 360
  Axis = (-3e-16,3e-16,1)
  Base = (0,0,0)
  Placement = pos=(0,0,0) rot=(0.57735,0.57735,0.57735;2.0944rad)
  Profile = -> Sketch116
  ReferenceAxis = -> Z_Axis
  Reversed = true
FEATURE [PartDesign::Body] Body014  label="PrimaryMirror"
  Group = -> [Local_CS,Local_CS001,Local_CS039,Sketch116,Revolution003]
  Origin = -> Origin
  Tip = -> Revolution003
COMPONENT P3 — recipe-attached ("MirrorClip", modeled in this document).
Construction recipe (the document's own serialized feature program — sketch geometry with constraints, then the solid features built on it; lengths are millimeters unless a unit is written):

FEATURE [Sketcher::SketchObject] Sketch042  label="MirrorClip_Profile"
  FullyConstrained = true
  MapMode = 5
  Placement = pos=(0,0,0) rot=(0.57735,0.57735,0.57735;2.0944rad)
  Support = -> [YZ_Plane034]
  expr: Constraints[16] = <<Common>>#<<Parameters>>.clipover + <<Common>>#<<Parameters>>.pri_mpad_z
  expr: Constraints[17] = <<Common>>#<<Parameters>>.clipthick
  expr: Constraints[18] = <<Common>>#<<Parameters>>.pri_mthick - <<Common>>#<<Parameters>>.zbracepos
  expr: Constraints[19] = <<Common>>#<<Parameters>>.clipwidth + 1
  expr: Constraints[29] = -<<Common>>#<<Parameters>>.pri_mpad_z
  expr: Constraints[41] = -<<Common>>#<<Parameters>>.pri_mpad_z + 0.5
  expr: Constraints[42] = <<Common>>#<<Parameters>>.pri_mpad_z
  expr: Constraints[6] = -<<Common>>#<<Parameters>>.datum_uppercell - <<Common>>#<<Parameters>>.pri_uthick + <<Common>>#<<Parameters>>.clipthick + 0.5
  sketch-geometry (18):
    g0: LineSegment StartX=0 StartY=0 StartZ=0 EndX=11 EndY=0 EndZ=0
    g1: LineSegment StartX=11 StartY=0 StartZ=0 EndX=11 EndY=35.5 EndZ=0
    g2: LineSegment StartX=11 StartY=35.5 StartZ=0 EndX=-8 EndY=35.5 EndZ=0
    g3: LineSegment StartX=-8 StartY=35.5 StartZ=0 EndX=-8 EndY=31.5 EndZ=0
    g4: LineSegment StartX=-8 StartY=31.5 StartZ=0 EndX=-2.5 EndY=31.5 EndZ=0
    g5: LineSegment StartX=-1 StartY=28.5 StartZ=0 EndX=-1 EndY=21.3851 EndZ=0
    g6: LineSegment StartX=-1 StartY=21.3851 StartZ=0 EndX=-2.73205 EndY=18.3851 EndZ=0
    g7: LineSegment StartX=-2.73205 StartY=16.3851 StartZ=0 EndX=0 EndY=11.6531 EndZ=0
    g8: LineSegment StartX=0 StartY=11.6531 StartZ=0 EndX=0 EndY=0 EndZ=0
    g9: LineSegment StartX=-3 StartY=17.3851 StartZ=0 EndX=11 EndY=17.3851 EndZ=0
    g10: ArcOfCircle CenterX=-1 CenterY=17.3851 CenterZ=0 NormalX=0 NormalY=0 NormalZ=1 AngleXU=0 Radius=2 StartAngle=2.61799 EndAngle=3.66519
    g11: GeomPoint X=-3 Y=17.3851 Z=0
    g12: GeomPoint X=-1 Y=31.5 Z=0
    g13: ArcOfEllipse CenterX=-2.5 CenterY=28.5 CenterZ=0 NormalX=0 NormalY=0 NormalZ=1 MajorRadius=3 MinorRadius=1.5 AngleXU=1.5708 StartAngle=4.71239 EndAngle=6.28319
    g14: LineSegment StartX=-2.5 StartY=31.5 StartZ=0 EndX=-2.5 EndY=25.5 EndZ=0
    g15: LineSegment StartX=-4 StartY=28.5 StartZ=0 EndX=-1 EndY=28.5 EndZ=0
    g16: GeomPoint X=-2.5 Y=31.0981 Z=0
    g17: GeomPoint X=-2.5 Y=25.9019 Z=0
  constraints (40):
    c: Coincident(g0,g1)
    c: Coincident(g1,g2)
    c: Horizontal(g0)
    c: Horizontal(g2)
    c: Vertical(g1)
    c: Coincident(g0,g-1)
    c: DistanceY(g1,g1) = 35.5
    c: Coincident(g3,g2)
    c: Vertical(g3)
    c: Coincident(g4,g3)
    c: Horizontal(g4)
    c: Vertical(g5)
    c: Coincident(g6,g5)
    c: Coincident(g8,g7)
    c: Coincident(g8,g0)
    c: Vertical(g8)
    c: DistanceX(g2,g-1) = 8
    c: DistanceY(g3,g3) = 4
    c: DistanceY(g11,g12) = 14.1149
    c: DistanceX(g0,g0) = 11
    c: Coincident(g9,g11)
    c: PointOnObject(g9,g1)
    c: Tangent(g6,g10) = -1.5708
    c: Tangent(g7,g10) = -1.5708
    c: Radius(g10) = 2
    c: PointOnObject(g10,g9)
    c: PointOnObject(g9,g10)
    c: PointOnObject(g12,g4)
    c: PointOnObject(g12,g5)
    c: DistanceX(g9) = -3
    c: Perpendicular(g1,g9)
    c: Angle(g7,g9) = 1.0472
    c: Angle(g9,g6) = 1.0472
    c: DistanceX(g5) = -1
    c: InternalAlignment(g14-g17 -> g13) x4
    c: Horizontal(g15)
    c: Tangent(g13,g4) = 1.5708
    c: Tangent(g13,g5) = 1.5708
    c: DistanceX(g13) = -2.5
    c: DistanceY(g5,g4) = 3
FEATURE [PartDesign::Pad] Pad022  label="MirrorClip_Profile_Pad"
  Direction = (1,-2e-16,3e-16)
  Length = 25
  Length2 = 100
  Midplane = true
  Placement = pos=(0,0,0) rot=(0.57735,0.57735,0.57735;2.0944rad)
  Profile = -> Sketch042
  Type = 0
  expr: Length = <<Common>>#<<Parameters>>.pri_fwidth
FEATURE [Sketcher::SketchObject] Sketch043  label="MirrorClip_RimCut_Sketch"
  ExternalGeometry = -> [Pad022]
  FullyConstrained = true
  MapMode = 5
  Support = -> [XY_Plane034]
  expr: Constraints[1] = <<Common>>#<<Parameters>>.pri_mdia
  expr: Constraints[25] = <<Common>>#<<Parameters>>.pri_fwidth
  expr: Constraints[2] = <<Common>>#<<Parameters>>.pri_mdia / 2 + <<Common>>#<<Parameters>>.pri_mpad_z
  sketch-geometry (9):
    g0: Circle CenterX=0 CenterY=-103 CenterZ=0 NormalX=0 NormalY=0 NormalZ=1 AngleXU=0 Radius=100
    g1: ArcOfCircle CenterX=-1.93e-14 CenterY=12.6399 CenterZ=0 NormalX=0 NormalY=0 NormalZ=1 AngleXU=0 Radius=20.6399 StartAngle=4.06184 EndAngle=5.36294
    g2: LineSegment StartX=-13.5 StartY=-9 StartZ=0 EndX=13.5 EndY=-9 EndZ=0
    g3: LineSegment StartX=-12.5 StartY=-3.78433 StartZ=0 EndX=-13.5 EndY=-3.78433 EndZ=0
    g4: LineSegment StartX=12.5 StartY=-3.78433 StartZ=0 EndX=13.5 EndY=-3.78433 EndZ=0
    g5: LineSegment StartX=13.5 StartY=-3.78433 StartZ=0 EndX=13.5 EndY=-9 EndZ=0
    g6: LineSegment StartX=-13.5 StartY=-3.78433 StartZ=0 EndX=-13.5 EndY=-9 EndZ=0
    g7: GeomPoint X=-12.5 Y=-3.78433 Z=0
    g8: GeomPoint X=12.5 Y=-3.78433 Z=0
  constraints (26):
    c: PointOnObject(g0,g-2)
    c: Diameter(g0) = 200
    c: DistanceY(g0,g-1) = 103
    c: Coincident(g3,g1)
    c: Horizontal(g3)
    c: Coincident(g4,g1)
    c: Coincident(g5,g4)
    c: Coincident(g6,g3)
    c: Coincident(g6,g2)
    c: Coincident(g2,g5)
    c: Horizontal(g4)
    c: Horizontal(g2)
    c: Vertical(g5)
    c: Vertical(g6)
    c: Equal(g4,g3)
    c: DistanceX(g4,g4) = 1
    c: Tangent(g1,g-4)
    c: DistanceY(g2,g-5) = 1
    c: PointOnObject(g7,g0)
    c: PointOnObject(g1,g-5)
    c: PointOnObject(g1,g-3)
    c: PointOnObject(g7,g1)
    c: Equal(g6,g5)
    c: PointOnObject(g8,g1)
    c: PointOnObject(g8,g0)
    c: DistanceX(g7,g8) = 25
FEATURE [PartDesign::Pocket] Pocket007  label="MirrorClip_RimCut"
  BaseFeature = -> Pad022
  Direction = (0,0,-1)
  Length = 5
  Length2 = 100
  Placement = pos=(0,0,0) rot=(0.57735,0.57735,0.57735;2.0944rad)
  Profile = -> Sketch043
  Reversed = true
  Type = 1
FEATURE [Sketcher::SketchObject] Sketch150  label="Mirrorclip_NutHole_Sketch"
  AttachmentOffset = pos=(0,0,24) rot=(0,0,1;0rad)
  ExternalGeometry = -> [Sketch043,Pocket007]
  FullyConstrained = false
  MapMode = 5
  Placement = pos=(0,0,24) rot=(0,0,1;0rad)
  Support = -> [XY_Plane034]
  sketch-geometry (14):
    g0: LineSegment StartX=-5.76329 StartY=8.51768 StartZ=0 EndX=-9.80474 EndY=8.51768 EndZ=0
    g1: LineSegment StartX=-9.80474 StartY=8.51768 StartZ=0 EndX=-11.8255 EndY=5.01768 EndZ=0
    g2: LineSegment StartX=-11.8255 StartY=5.01768 StartZ=0 EndX=-9.80474 EndY=1.51768 EndZ=0
    g3: LineSegment StartX=-9.80474 StartY=1.51768 StartZ=0 EndX=-5.76329 EndY=1.51768 EndZ=0
    g4: LineSegment StartX=-5.76329 StartY=1.51768 StartZ=0 EndX=-3.74256 EndY=5.01768 EndZ=0
    g5: LineSegment StartX=-3.74256 StartY=5.01768 StartZ=0 EndX=-5.76329 EndY=8.51768 EndZ=0
    g6: Circle CenterX=-7.78401 CenterY=5.01768 CenterZ=0 NormalX=0 NormalY=0 NormalZ=1 AngleXU=0 Radius=4.04145
    g7: LineSegment StartX=-2.02073 StartY=9.13987 StartZ=0 EndX=2.02073 EndY=9.13987 EndZ=0
    g8: LineSegment StartX=2.02073 StartY=9.13987 StartZ=0 EndX=4.04145 EndY=12.6399 EndZ=0
    g9: LineSegment StartX=4.04145 StartY=12.6399 StartZ=0 EndX=2.02073 EndY=16.1399 EndZ=0
    g10: LineSegment StartX=2.02073 StartY=16.1399 StartZ=0 EndX=-2.02073 EndY=16.1399 EndZ=0
    g11: LineSegment StartX=-2.02073 StartY=16.1399 StartZ=0 EndX=-4.04145 EndY=12.6399 EndZ=0
    g12: LineSegment StartX=-4.04145 StartY=12.6399 StartZ=0 EndX=-2.02073 EndY=9.13987 EndZ=0
    g13: Circle CenterX=-1.93e-14 CenterY=12.6399 CenterZ=0 NormalX=0 NormalY=0 NormalZ=1 AngleXU=0 Radius=4.04145
  constraints (32):
    c: Coincident(g0,g1)
    c: Coincident(g1,g2)
    c: Coincident(g2,g3)
    c: Coincident(g3,g4)
    c: Coincident(g4,g5)
    c: Coincident(g5,g0)
    c: Equal(g0, g1-g5) x5
    c: PointOnObject(g0,g6)
    c: PointOnObject(g1,g6)
    c: PointOnObject(g2,g6)
    c: PointOnObject(g3,g6)
    c: PointOnObject(g4,g6)
    c: PointOnObject(g5,g6)
    c: Coincident(g7,g8)
    c: Coincident(g8,g9)
    c: Coincident(g9,g10)
    c: Coincident(g10,g11)
    c: Coincident(g11,g12)
    c: Coincident(g12,g7)
    c: Equal(g7, g8-g12) x5
    c: PointOnObject(g7,g13)
    c: PointOnObject(g8,g13)
    c: PointOnObject(g9,g13)
    c: PointOnObject(g10,g13)
    c: PointOnObject(g11,g13)
    c: PointOnObject(g12,g13)
    c: Coincident(g13,g-4)
    c: Equal(g13,g6)
    c: DistanceY(g0,g-5) = 2.48232
    c: Horizontal(g10)
    c: DistanceY(g12,g11) = 7
    c: Horizontal(g0)
FEATURE [Sketcher::SketchObject] Sketch207  label="MirrorClip_SideCut_Sketch"
  ExternalGeometry = -> [Pocket007]
  FullyConstrained = true
  MapMode = 5
  Placement = pos=(0,0,0) rot=(1,0,0;1.5708rad)
  Support = -> [XZ_Plane034]
  expr: Constraints[15] = <<Common>>#<<Parameters>>.pri_fwidth
  sketch-geometry (9):
    g0: LineSegment StartX=-13.5 StartY=25.7321 StartZ=0 EndX=-12.5 EndY=24 EndZ=0
    g1: LineSegment StartX=-12.5 StartY=24 StartZ=0 EndX=-12.5 EndY=-1 EndZ=0
    g2: LineSegment StartX=-12.5 StartY=-1 StartZ=0 EndX=-13.5 EndY=-1 EndZ=0
    g3: LineSegment StartX=-13.5 StartY=-1 StartZ=0 EndX=-13.5 EndY=25.7321 EndZ=0
    g4: LineSegment StartX=13.5 StartY=25.7321 StartZ=0 EndX=12.5 EndY=24 EndZ=0
    g5: LineSegment StartX=12.5 StartY=24 StartZ=0 EndX=12.5 EndY=-1 EndZ=0
    g6: LineSegment StartX=12.5 StartY=-1 StartZ=0 EndX=13.5 EndY=-1 EndZ=0
    g7: LineSegment StartX=13.5 StartY=-1 StartZ=0 EndX=13.5 EndY=25.7321 EndZ=0
    g8: GeomPoint X=12.5 Y=24 Z=0
  constraints (23):
    c: Coincident(g0,g1)
    c: Coincident(g1,g2)
    c: Coincident(g2,g3)
    c: Coincident(g3,g0)
    c: Horizontal(g2)
    c: Vertical(g1)
    c: Vertical(g3)
    c: Coincident(g4,g5)
    c: Coincident(g5,g6)
    c: Coincident(g6,g7)
    c: Coincident(g7,g4)
    c: Horizontal(g6)
    c: Vertical(g7)
    c: Symmetric(g1,g5,g-2)
    c: Symmetric(g0,g4,g-2)
    c: DistanceX(g0,g4) = 25
    c: Symmetric(g4,g0,g-2)
    c: Angle(g5,g4) = 2.61799
    c: DistanceY(g5) = -1
    c: DistanceX(g-3,g6) = 1
    c: PointOnObject(g8,g-4)
    c: PointOnObject(g8,g4)
    c: DistanceY(g8) = 24
FEATURE [Sketcher::SketchObject] Sketch287  label="MirrorClip_MountHole_Sketch"
  FullyConstrained = true
  MapMode = 5
  Placement = pos=(0,0,0) rot=(0,1,0;3.14159rad)
  Support = -> [XY_Plane034]
  expr: Constraints[1] = <<Common>>#<<Parameters>>.pri_fwidth - <<Common>>#<<Parameters>>.clipbolt * 2.5
  expr: Constraints[2] = <<Common>>#<<Parameters>>.clipwidth / 2
  expr: Constraints[3] = <<Common>>#<<Parameters>>.clipbolt
  sketch-geometry (2):
    g0: Circle CenterX=-7.5 CenterY=5 CenterZ=0 NormalX=0 NormalY=0 NormalZ=1 AngleXU=0 Radius=2
    g1: Circle CenterX=7.5 CenterY=5 CenterZ=0 NormalX=0 NormalY=0 NormalZ=1 AngleXU=0 Radius=2
  constraints (5):
    c: Symmetric(g0,g1,g-2)
    c: DistanceX(g0,g1) = 15
    c: DistanceY(g0) = 5
    c: Diameter(g0) = 4
    c: Equal(g0,g1)
FEATURE [PartDesign::CoordinateSystem] Local_CS086  label="LCS_MirrorClip_Base"
  AttacherType = Attacher::AttachEngine3D
  AttachmentOffset = pos=(0,0,0) rot=(0,0,1;1.5708rad)
  MapMode = 45
  Placement = pos=(-9e-15,5,0) rot=(0,0,1;3.14159rad)
  Support = -> [Sketch287]
FEATURE [PartDesign::CoordinateSystem] Local_CS088  label="LCS_MirrorClip_Mount_2"
  AttacherType = Attacher::AttachEngine3D
  MapMode = 11
  Placement = pos=(-7.5,5,0) rot=(0.707107,0.707107,0;3.14159rad)
  Support = -> [Sketch287]
FEATURE [PartDesign::CoordinateSystem] Local_CS087  label="LCS_MirrorClip_Mount_1"
  AttacherType = Attacher::AttachEngine3D
  MapMode = 11
  Placement = pos=(7.5,5,0) rot=(0.707107,0.707107,0;3.14159rad)
  Support = -> [Sketch287]
FEATURE [PartDesign::Hole] Hole056  label="MirrorClip_MountHole"
  BaseFeature = -> Pocket007
  CustomThreadClearance = 0.25
  Depth = 95.7371
  DepthType = 1
  Diameter = 3.55
  DrillForDepth = false
  DrillPoint = 1
  DrillPointAngle = 118
  HoleCutCountersinkAngle = 90
  HoleCutCustomValues = false
  HoleCutDepth = 0
  HoleCutDiameter = 6.1
  HoleCutType = 0
  ModelThread = true
  Placement = pos=(0,0,0) rot=(0.57735,0.57735,0.57735;2.0944rad)
  Profile = -> Sketch287
  Tapered = false
  TaperedAngle = 90
  ThreadClass = 0
  ThreadDepth = 95.7371
  ThreadDepthType = 0
  ThreadDirection = 0
  ThreadFit = 0
  ThreadSize = 11
  ThreadType = 1
  Threaded = true
  UseCustomThreadClearance = true
FEATURE [PartDesign::Chamfer] Chamfer  label="MirrorClip_Chamfer"
  Angle = 45
  Base = -> Hole056 [Edge13,Edge32,Edge21,Edge33,Edge31]
  BaseFeature = -> Hole056
  ChamferType = 0
  FlipDirection = false
  Placement = pos=(0,0,0) rot=(0.57735,0.57735,0.57735;2.0944rad)
  Size = 0.4
  Size2 = 1
  SupportTransform = false
  UseAllEdges = false
FEATURE [PartDesign::Body] Body022  label="MirrorClip"
  Group = -> [Sketch042,Pad022,Sketch043,Pocket007,Local_CS086,Local_CS087,Local_CS088,Sketch150,Sketch207,Sketch287,Hole056,Chamfer]
  Origin = -> Origin034
  Placement = pos=(72.832,72.832,-31) rot=(0,0,-1;0.785398rad)
  Tip = -> Chamfer
  expr: .Placement.Base.x = (<<Common>>#<<Parameters>>.pri_mdia / 2 + <<Common>>#<<Parameters>>.pri_mpad_z) / sqrt(2)
  expr: .Placement.Base.y = (<<Common>>#<<Parameters>>.pri_mdia / 2 + <<Common>>#<<Parameters>>.pri_mpad_z) / sqrt(2)
  expr: .Placement.Base.z = <<Common>>#<<Parameters>>.datum_uppercell + <<Common>>#<<Parameters>>.pri_uthick
COMPONENT P4 — recipe-attached ("PrimaryMirrorCover", modeled in this document).
Construction recipe (the document's own serialized feature program — sketch geometry with constraints, then the solid features built on it; lengths are millimeters unless a unit is written):

FEATURE [Sketcher::SketchObject] Sketch288
  FullyConstrained = true
  MapMode = 5
  Placement = pos=(0,0,0) rot=(1,0,0;1.5708rad)
  Support = -> [XZ_Plane036]
  expr: Constraints[21] = <<Common>>#<<Parameters>>.pri_mdia / 2
  sketch-geometry (14):
    g0: LineSegment StartX=0 StartY=5.8 StartZ=0 EndX=95.8971 EndY=5.8 EndZ=0
    g1: LineSegment StartX=95.8971 StartY=5.8 StartZ=0 EndX=102.2 EndY=-0.502944 EndZ=0
    g2: LineSegment StartX=102.2 StartY=-0.502944 StartZ=0 EndX=102.2 EndY=-16.9392 EndZ=0
    g3: LineSegment StartX=102.2 StartY=-16.9392 StartZ=0 EndX=101 EndY=-16.9392 EndZ=0
    g4: LineSegment StartX=101 StartY=-16.9392 StartZ=0 EndX=99.3608 EndY=-14.1 EndZ=0
    g5: LineSegment StartX=99.3608 StartY=-12.9 StartZ=0 EndX=101 EndY=-10.0608 EndZ=0
    g6: LineSegment StartX=101 StartY=-10.0608 StartZ=0 EndX=101 EndY=-1 EndZ=0
    g7: LineSegment StartX=101 StartY=-1 StartZ=0 EndX=95 EndY=5 EndZ=0
    g8: LineSegment StartX=95 StartY=5 StartZ=0 EndX=0 EndY=5 EndZ=0
    g9: LineSegment StartX=0 StartY=5 StartZ=0 EndX=0 EndY=5.8 EndZ=0
    g10: GeomPoint X=100 Y=0 Z=0
    g11: LineSegment StartX=95 StartY=5 StartZ=0 EndX=95.8485 EndY=5.84853 EndZ=0
    g12: ArcOfCircle CenterX=100.4 CenterY=-13.5 CenterZ=0 NormalX=0 NormalY=0 NormalZ=1 AngleXU=0 Radius=1.2 StartAngle=2.61799 EndAngle=3.66519
    g13: LineSegment StartX=100.4 StartY=-13.5 StartZ=0 EndX=99.2 EndY=-13.5 EndZ=0
  constraints (40):
    c: PointOnObject(g0,g-2)
    c: Horizontal(g0)
    c: Coincident(g1,g0)
    c: Coincident(g2,g1)
    c: Vertical(g2)
    c: Coincident(g3,g2)
    c: Coincident(g4,g3)
    c: Coincident(g6,g5)
    c: Vertical(g6)
    c: Coincident(g7,g6)
    c: Coincident(g8,g7)
    c: Horizontal(g8)
    c: Coincident(g9,g8)
    c: Coincident(g9,g0)
    c: Vertical(g9)
    c: DistanceY(g-1,g8) = 5
    c: DistanceY(g9,g9) = 0.8
    c: Parallel(g7,g1)
    c: Angle(g-1,g1) = 2.35619
    c: PointOnObject(g10,g7)
    c: PointOnObject(g10,g-1)
    c: DistanceX(g10) = 100
    c: DistanceX(g10,g6) = 1
    c: DistanceX(g6,g1) = 1.2
    c: Coincident(g11,g7)
    c: PointOnObject(g11,g1)
    c: Perpendicular(g1,g11)
    c: Distance(g11) = 1.2
    c: Angle(g6,g5) = 2.61799
    c: DistanceX(g3,g3) = 1.2
    c: Horizontal(g3)
    c: Angle(g3,g4) = 2.0944
    c: Radius(g12) = 1.2
    c: Tangent(g12,g5) = 1.5708
    c: Tangent(g12,g4) = 1.5708
    c: Coincident(g13,g12)
    c: PointOnObject(g13,g12)
    c: Horizontal(g13)
    c: DistanceX(g13,g10) = 0.8
    c: DistanceY(g12,g10) = 13.5
FEATURE [PartDesign::Revolution] Revolution004
  Angle = 360
  Axis = (1e-16,1e-16,1)
  Base = (0,0,0)
  Placement = pos=(0,0,0) rot=(1,0,0;1.5708rad)
  Profile = -> Sketch288
  ReferenceAxis = -> Z_Axis036
  Reversed = true
FEATURE [Sketcher::SketchObject] Sketch289
  FullyConstrained = true
  MapMode = 5
  Support = -> [XY_Plane036]
  expr: Constraints[14] = <<Common>>#<<Parameters>>.pri_fwidth + 2
  expr: Constraints[1] = <<Common>>#<<Parameters>>.pri_mdia
  expr: Constraints[20] = <<Common>>#<<Parameters>>.clipover + 1
  sketch-geometry (23):
    g0: Circle CenterX=0 CenterY=0 CenterZ=0 NormalX=0 NormalY=0 NormalZ=1 AngleXU=0 Radius=100
    g1: LineSegment StartX=-13.5 StartY=99.0846 StartZ=0 EndX=-13.5 EndY=-99.0846 EndZ=0
    g2: LineSegment StartX=13.5 StartY=99.0846 StartZ=0 EndX=13.5 EndY=-99.0846 EndZ=0
    g3: LineSegment StartX=99.0846 StartY=13.5 StartZ=0 EndX=-99.0846 EndY=13.5 EndZ=0
    g4: LineSegment StartX=99.0846 StartY=-13.5 StartZ=0 EndX=-99.0846 EndY=-13.5 EndZ=0
    g5: LineSegment StartX=-13.5 StartY=94 StartZ=0 EndX=13.5 EndY=94 EndZ=0
    g6: GeomPoint X=0 Y=100 Z=0
    g7: ArcOfCircle CenterX=0 CenterY=114.464 CenterZ=0 NormalX=0 NormalY=0 NormalZ=1 AngleXU=0 Radius=20.4642 StartAngle=3.99198 EndAngle=5.43279
    g8: LineSegment StartX=-13.5 StartY=99.0846 StartZ=0 EndX=-13.5 EndY=114.464 EndZ=0
    g9: LineSegment StartX=13.5 StartY=99.0846 StartZ=0 EndX=13.5 EndY=114.464 EndZ=0
    g10: LineSegment StartX=13.5 StartY=114.464 StartZ=0 EndX=-13.5 EndY=114.464 EndZ=0
    g11: ArcOfCircle CenterX=114.464 CenterY=1.8e-15 CenterZ=0 NormalX=0 NormalY=0 NormalZ=1 AngleXU=0 Radius=20.4642 StartAngle=2.42119 EndAngle=3.862
    g12: ArcOfCircle CenterX=-114.464 CenterY=3.7e-15 CenterZ=0 NormalX=0 NormalY=0 NormalZ=1 AngleXU=0 Radius=20.4642 StartAngle=5.56278 EndAngle=7.00359
    g13: ArcOfCircle CenterX=-8.6e-15 CenterY=-114.464 CenterZ=0 NormalX=0 NormalY=0 NormalZ=1 AngleXU=0 Radius=20.4642 StartAngle=0.850391 EndAngle=2.2912
    g14: LineSegment StartX=-99.0846 StartY=13.5 StartZ=0 EndX=-114.464 EndY=13.5 EndZ=0
    g15: LineSegment StartX=-114.464 StartY=13.5 StartZ=0 EndX=-114.464 EndY=-13.5 EndZ=0
    g16: LineSegment StartX=-114.464 StartY=-13.5 StartZ=0 EndX=-99.0846 EndY=-13.5 EndZ=0
    g17: LineSegment StartX=99.0846 StartY=13.5 StartZ=0 EndX=114.464 EndY=13.5 EndZ=0
    g18: LineSegment StartX=114.464 StartY=13.5 StartZ=0 EndX=114.464 EndY=-13.5 EndZ=0
    g19: LineSegment StartX=114.464 StartY=-13.5 StartZ=0 EndX=99.0846 EndY=-13.5 EndZ=0
    g20: LineSegment StartX=-13.5 StartY=-99.0846 StartZ=0 EndX=-13.5 EndY=-114.464 EndZ=0
    g21: LineSegment StartX=-13.5 StartY=-114.464 StartZ=0 EndX=13.5 EndY=-114.464 EndZ=0
    g22: LineSegment StartX=13.5 StartY=-114.464 StartZ=0 EndX=13.5 EndY=-99.0846 EndZ=0
  constraints (67):
    c: Coincident(g0,g-1)
    c: Diameter(g0) = 200
    c: Vertical(g1)
    c: Vertical(g2)
    c: Horizontal(g3)
    c: Horizontal(g4)
    c: Symmetric(g1,g2,g-2)
    c: PointOnObject(g1,g0)
    c: PointOnObject(g2,g0)
    c: PointOnObject(g3,g0)
    c: PointOnObject(g4,g0)
    c: Symmetric(g3,g4,g-1)
    c: PointOnObject(g3,g0)
    c: PointOnObject(g1,g0)
    c: DistanceX(g1,g2) = 27
    c: PointOnObject(g5,g1)
    c: PointOnObject(g5,g2)
    c: Horizontal(g5)
    c: PointOnObject(g6,g-2)
    c: PointOnObject(g6,g0)
    c: DistanceY(g5,g6) = 6
    c: PointOnObject(g7,g-2)
    c: Coincident(g7,g1)
    c: PointOnObject(g7,g0)
    c: Tangent(g7,g5)
    c: Coincident(g8,g7)
    c: Vertical(g8)
    c: Coincident(g9,g7)
    c: Vertical(g9)
    c: Coincident(g10,g9)
    c: Coincident(g10,g8)
    c: Horizontal(g10)
    c: Coincident(g11,g3)
    c: Coincident(g11,g4)
    c: Equal(g11,g7)
    c: Coincident(g12,g3)
    c: Coincident(g12,g4)
    c: Coincident(g13,g1)
    c: Coincident(g13,g2)
    c: Equal(g13,g12)
    c: Equal(g12,g7)
    c: Coincident(g14,g12)
    c: Horizontal(g14)
    c: Coincident(g15,g14)
    c: Vertical(g15)
    c: Coincident(g16,g15)
    c: Coincident(g16,g12)
    c: Horizontal(g16)
    c: Coincident(g17,g11)
    c: Horizontal(g17)
    c: Coincident(g18,g17)
    c: Vertical(g18)
    c: Coincident(g19,g18)
    c: Coincident(g19,g11)
    c: Horizontal(g19)
    c: Coincident(g20,g13)
    c: Vertical(g20)
    c: Coincident(g21,g20)
    c: Horizontal(g21)
    c: Coincident(g22,g21)
    c: Coincident(g22,g13)
    c: Vertical(g22)
    c: PointOnObject(g13,g21)
    c: PointOnObject(g11,g18)
    c: PointOnObject(g12,g15)
    c: PointOnObject(g7,g10)
    c: Equal(g18,g10)
FEATURE [PartDesign::Pocket] Pocket
  BaseFeature = -> Revolution004
  Direction = (0,0,-1)
  Length = 5
  Length2 = 5
  Midplane = true
  Placement = pos=(0,0,0) rot=(1,0,0;1.5708rad)
  Profile = -> Sketch289
  ReferenceAxis = -> Sketch289 [N_Axis]
  Type = 1
FEATURE [Sketcher::SketchObject] Sketch290
  AttachmentOffset = pos=(0,0,-6) rot=(0,0,1;0.785398rad)
  ExternalGeometry = -> [Sketch289]
  FullyConstrained = true
  MapMode = 5
  Placement = pos=(0,0,-6) rot=(0,0,1;0.785398rad)
  Support = -> [XY_Plane036]
  expr: Constraints[38] = <<Common>>#<<Parameters>>.pri_mdia / 2
  expr: Constraints[56] = .Constraints.TabWidth
  expr: Constraints[57] = .Constraints.TabWidth
  expr: Constraints[58] = .Constraints.TabWidth
  expr: Constraints[59] = .Constraints.TabWidth
  sketch-geometry (22):
    g0: ArcOfCircle CenterX=0 CenterY=0 CenterZ=0 NormalX=0 NormalY=0 NormalZ=1 AngleXU=0 Radius=110 StartAngle=2.74226 EndAngle=3.54092
    g1: ArcOfCircle CenterX=0 CenterY=0 CenterZ=0 NormalX=0 NormalY=0 NormalZ=1 AngleXU=0 Radius=110 StartAngle=1.17147 EndAngle=1.97013
    g2: ArcOfCircle CenterX=0 CenterY=0 CenterZ=0 NormalX=0 NormalY=0 NormalZ=1 AngleXU=0 Radius=110 StartAngle=5.88386 EndAngle=6.68251
    g3: ArcOfCircle CenterX=0 CenterY=0 CenterZ=0 NormalX=0 NormalY=0 NormalZ=1 AngleXU=0 Radius=110 StartAngle=4.31306 EndAngle=5.11172
    g4: LineSegment StartX=-101.345 StartY=42.768 StartZ=0 EndX=-82.919 EndY=34.992 EndZ=0
    g5: LineSegment StartX=-82.919 StartY=34.992 StartZ=0 EndX=-34.992 EndY=82.919 EndZ=0
    g6: LineSegment StartX=-34.992 StartY=82.919 StartZ=0 EndX=-42.768 EndY=101.345 EndZ=0
    g7: LineSegment StartX=42.768 StartY=101.345 StartZ=0 EndX=34.992 EndY=82.919 EndZ=0
    g8: LineSegment StartX=34.992 StartY=82.919 StartZ=0 EndX=82.919 EndY=34.992 EndZ=0
    g9: LineSegment StartX=82.919 StartY=34.992 StartZ=0 EndX=101.345 EndY=42.768 EndZ=0
    g10: LineSegment StartX=101.345 StartY=-42.768 StartZ=0 EndX=82.919 EndY=-34.992 EndZ=0
    g11: LineSegment StartX=82.919 StartY=-34.992 StartZ=0 EndX=34.992 EndY=-82.919 EndZ=0
    g12: LineSegment StartX=34.992 StartY=-82.919 StartZ=0 EndX=42.768 EndY=-101.345 EndZ=0
    g13: LineSegment StartX=-42.768 StartY=-101.345 StartZ=0 EndX=-34.992 EndY=-82.919 EndZ=0
    g14: LineSegment StartX=-34.992 StartY=-82.919 StartZ=0 EndX=-82.919 EndY=-34.992 EndZ=0
    g15: LineSegment StartX=-82.919 StartY=-34.992 StartZ=0 EndX=-101.345 EndY=-42.768 EndZ=0
    g16: GeomPoint X=38.88 Y=92.1322 Z=0
    g17: GeomPoint X=92.1322 Y=38.88 Z=0
    g18: Circle CenterX=0 CenterY=0 CenterZ=0 NormalX=0 NormalY=0 NormalZ=1 AngleXU=0 Radius=100
    g19: GeomPoint X=-38.88 Y=92.1322 Z=0
    g20: GeomPoint X=-92.1322 Y=-38.88 Z=0
    g21: GeomPoint X=38.88 Y=-92.1322 Z=0
  constraints (60):
    c: Coincident(g0,g-1)
    c: Coincident(g1,g0)
    c: Coincident(g2,g0)
    c: Coincident(g3,g0)
    c: Coincident(g4,g0)
    c: Coincident(g5,g4)
    c: Coincident(g6,g5)
    c: Coincident(g6,g1)
    c: Coincident(g7,g1)
    c: Coincident(g8,g7)
    c: Coincident(g9,g8)
    c: Coincident(g9,g2)
    c: Coincident(g10,g2)
    c: Coincident(g11,g10)
    c: Coincident(g12,g11)
    c: Coincident(g12,g3)
    c: Coincident(g13,g3)
    c: Coincident(g14,g13)
    c: Coincident(g15,g14)
    c: Coincident(g15,g0)
    c: Equal(g3,g0)
    c: Equal(g0,g1)
    c: Equal(g1,g2)
    c: PointOnObject(g0,g6)
    c: PointOnObject(g0,g15)
    c: PointOnObject(g0,g9)
    c: PointOnObject(g0,g12)
    c: Equal(g14,g5)
    c: Equal(g5,g8)
    c: Equal(g8,g11)
    c: Equal(g6,g4)
    c: Equal(g9,g7)
    c: Equal(g13,g15)
    c: Equal(g12,g10)
    c: Equal(g13,g10)
    c: Equal(g10,g7)
    c: Equal(g4,g7)
    c: PointOnObject(g17,g9)
    c: Distance(g17,g0) = 100
    c: Coincident(g18,g0)
    c: PointOnObject(g17,g18)
    c: PointOnObject(g0,g13)
    c: PointOnObject(g0,g7)
    c: PointOnObject(g0,g10)
    c: PointOnObject(g0,g4)
    c: PointOnObject(g16,g7)
    c: PointOnObject(g16,g18)
    c: Distance(g16,g1) = 10
    c: Distance(g7,g16) = 10
    c: Distance(g16,g-8) = 25  'TabWidth'
    c: PointOnObject(g19,g6)
    c: PointOnObject(g19,g18)
    c: PointOnObject(g20,g15)
    c: PointOnObject(g21,g12)
    c: PointOnObject(g20,g18)
    c: PointOnObject(g21,g18)
    c: Distance(g-3,g17) = 25
    c: Distance(g-4,g19) = 25
    c: Distance(g20,g-5) = 25
    c: Distance(g21,g-6) = 25
FEATURE [PartDesign::Pocket] Pocket037
  BaseFeature = -> Pocket
  Direction = (0,0,-1)
  Length = 5
  Length2 = 5
  Placement = pos=(0,0,0) rot=(1,0,0;1.5708rad)
  Profile = -> Sketch290
  ReferenceAxis = -> Sketch290 [N_Axis]
  Type = 1
FEATURE [Sketcher::SketchObject] Sketch291
  AttachmentOffset = pos=(0,0,0) rot=(0,1,0;0.785398rad)
  FullyConstrained = true
  MapMode = 5
  Placement = pos=(0,0,0) rot=(0.862856,0.357407,0.357407;1.71777rad)
  Support = -> [XZ_Plane036]
  expr: Constraints[4] = <<Common>>#<<Parameters>>.pri_mdia / 2 + 0.6
  sketch-geometry (3):
    g0: LineSegment StartX=15 StartY=5 StartZ=0 EndX=95.6 EndY=5 EndZ=0
    g1: LineSegment StartX=15 StartY=5 StartZ=0 EndX=100.6 EndY=0 EndZ=0
    g2: LineSegment StartX=100.6 StartY=0 StartZ=0 EndX=95.6 EndY=5 EndZ=0
  constraints (9):
    c: Horizontal(g0)
    c: Coincident(g1,g0)
    c: PointOnObject(g1,g-1)
    c: DistanceY(g0) = 5
    c: DistanceX(g1) = 100.6
    c: Coincident(g2,g1)
    c: Coincident(g0,g2)
    c: Angle(g2,g-1) = 0.785398
    c: DistanceX(g0) = 15
FEATURE [PartDesign::Pad] Pad
  BaseFeature = -> Pocket037
  Direction = (0.707107,-0.707107,-1e-16)
  Length = 1.2
  Length2 = 10
  Midplane = true
  Placement = pos=(0,0,0) rot=(1,0,0;1.5708rad)
  Profile = -> Sketch291
  ReferenceAxis = -> Sketch291 [N_Axis]
  Type = 0
FEATURE [PartDesign::PolarPattern] PolarPattern
  Angle = 360
  Axis = -> Z_Axis036
  BaseFeature = -> Pad
  Occurrences = 12
  Originals = -> [Pad]
  Placement = pos=(0,0,0) rot=(1,0,0;1.5708rad)
FEATURE [PartDesign::Body] Body023  label="PrimaryMirrorCover"
  Group = -> [Sketch288,Revolution004,Sketch289,Pocket,Sketch290,Pocket037,Sketch291,Pad,PolarPattern]
  Origin = -> Origin036
  Placement = pos=(0,0,0) rot=(0,0,1;0.785398rad)
  Tip = -> PolarPattern
PROVENANCE & LICENSES
A FreeCAD (.FCStd) document from a public repository crawl; recipes are the document's own serialized feature recipes (and, for linked parts, companion documents' recipes).
License: as declared in the source repository (recorded in the dataset sidecar).
